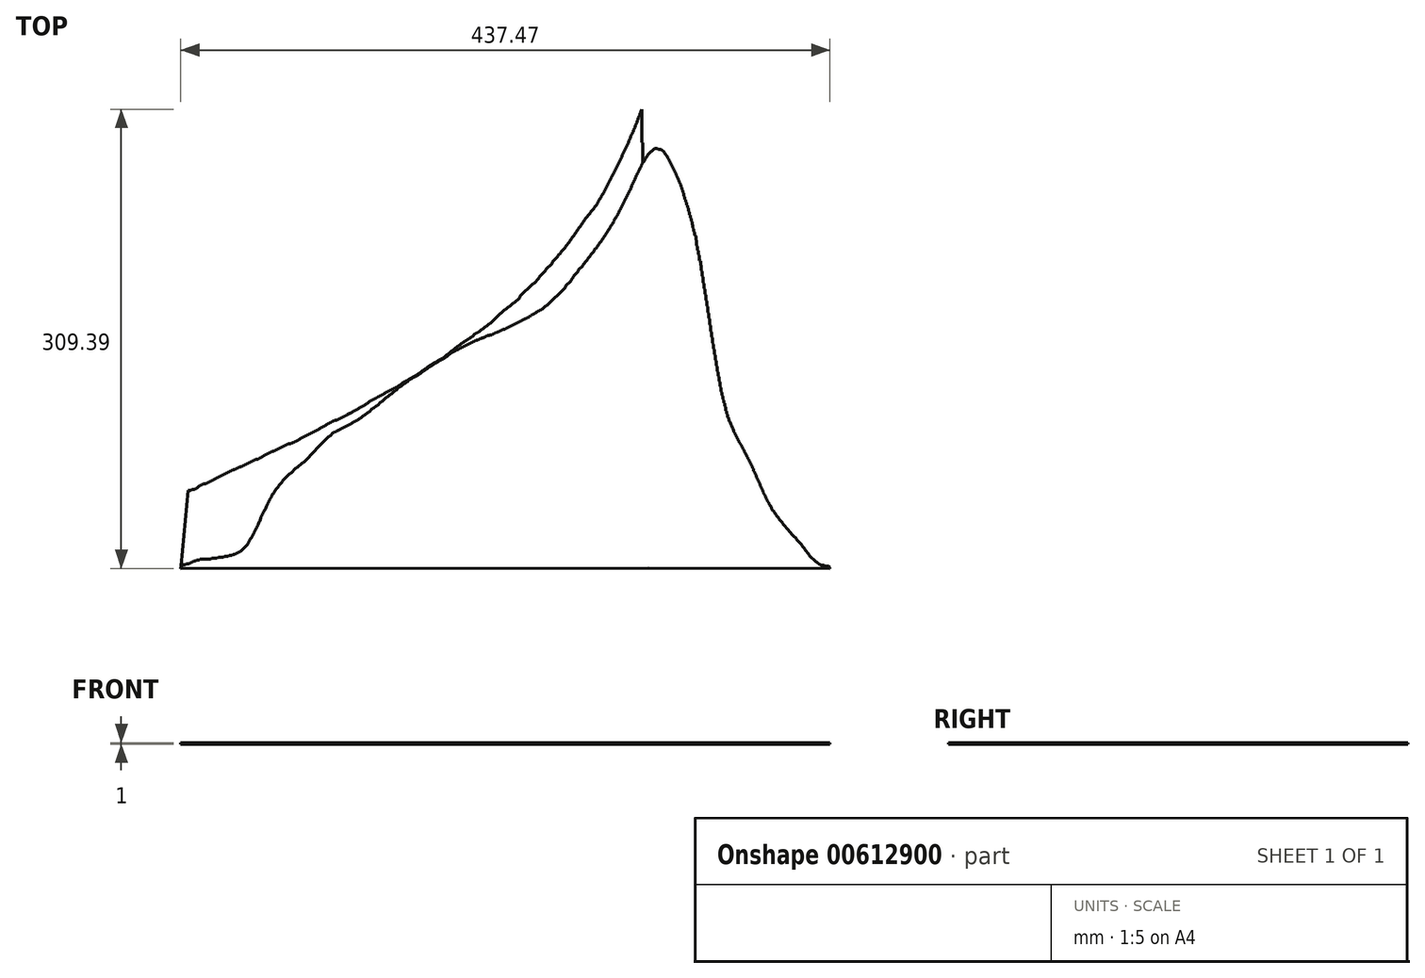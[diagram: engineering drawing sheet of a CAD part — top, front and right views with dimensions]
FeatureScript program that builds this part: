
annotation { "Feature Type Name" : "Feature", "Feature Type Description" : "" }
export const myFeature = defineFeature(function(context is Context, id is Id, definition is map)
    precondition{}
    {
        {
            var Q0;
            Q0=qCreatedBy(makeId("Top.planeOp"),FACE);
            var sketch = newSketch(context, id + "F0", { "sketchPlane" : qUnion([Q0])});
            skLineSegment(sketch, "E0", {"start": v(51.13, 44.28) * mm, "end": v(56.13, 96.91) * mm});
            skLineSegment(sketch, "E1", {"start": v(56.13, 96.91) * mm, "end": v(58.05, 96.91) * mm});
            skLineSegment(sketch, "E2", {"start": v(58.05, 96.91) * mm, "end": v(58.66, 97.6) * mm});
            skLineSegment(sketch, "E3", {"start": v(58.66, 97.6) * mm, "end": v(60.56, 97.6) * mm});
            skLineSegment(sketch, "E4", {"start": v(60.56, 97.6) * mm, "end": v(61.2, 98.2) * mm});
            skLineSegment(sketch, "E5", {"start": v(61.2, 98.2) * mm, "end": v(61.81, 98.2) * mm});
            skLineSegment(sketch, "E6", {"start": v(61.81, 98.2) * mm, "end": v(63.7, 100.09) * mm});
            skLineSegment(sketch, "E7", {"start": v(63.7, 100.09) * mm, "end": v(64.32, 100.09) * mm});
            skLineSegment(sketch, "E8", {"start": v(64.32, 100.09) * mm, "end": v(64.95, 100.72) * mm});
            skLineSegment(sketch, "E9", {"start": v(64.95, 100.72) * mm, "end": v(65.58, 100.72) * mm});
            skLineSegment(sketch, "E10", {"start": v(65.58, 100.72) * mm, "end": v(66.2, 101.35) * mm});
            skLineSegment(sketch, "E11", {"start": v(66.2, 101.35) * mm, "end": v(68.08, 101.35) * mm});
            skLineSegment(sketch, "E12", {"start": v(68.08, 101.35) * mm, "end": v(68.71, 101.98) * mm});
            skLineSegment(sketch, "E13", {"start": v(68.71, 101.98) * mm, "end": v(69.35, 101.98) * mm});
            skLineSegment(sketch, "E14", {"start": v(69.35, 101.98) * mm, "end": v(69.97, 102.6) * mm});
            skLineSegment(sketch, "E15", {"start": v(69.97, 102.6) * mm, "end": v(70.6, 102.6) * mm});
            skLineSegment(sketch, "E16", {"start": v(70.6, 102.6) * mm, "end": v(71.23, 103.23) * mm});
            skLineSegment(sketch, "E17", {"start": v(71.23, 103.23) * mm, "end": v(71.85, 103.23) * mm});
            skLineSegment(sketch, "E18", {"start": v(71.85, 103.23) * mm, "end": v(72.48, 103.86) * mm});
            skLineSegment(sketch, "E19", {"start": v(72.48, 103.86) * mm, "end": v(73.11, 103.86) * mm});
            skLineSegment(sketch, "E20", {"start": v(73.11, 103.86) * mm, "end": v(73.73, 104.49) * mm});
            skLineSegment(sketch, "E21", {"start": v(73.73, 104.49) * mm, "end": v(74.35, 104.49) * mm});
            skLineSegment(sketch, "E22", {"start": v(74.35, 104.49) * mm, "end": v(74.98, 105.11) * mm});
            skLineSegment(sketch, "E23", {"start": v(74.98, 105.11) * mm, "end": v(75.62, 105.11) * mm});
            skLineSegment(sketch, "E24", {"start": v(75.62, 105.11) * mm, "end": v(76.24, 105.74) * mm});
            skLineSegment(sketch, "E25", {"start": v(76.24, 105.74) * mm, "end": v(76.87, 105.74) * mm});
            skLineSegment(sketch, "E26", {"start": v(76.87, 105.74) * mm, "end": v(77.49, 106.37) * mm});
            skLineSegment(sketch, "E27", {"start": v(77.49, 106.37) * mm, "end": v(78.12, 106.37) * mm});
            skLineSegment(sketch, "E28", {"start": v(78.12, 106.37) * mm, "end": v(78.75, 107) * mm});
            skLineSegment(sketch, "E29", {"start": v(78.75, 107) * mm, "end": v(79.39, 107) * mm});
            skLineSegment(sketch, "E30", {"start": v(79.39, 107) * mm, "end": v(80.01, 107.61) * mm});
            skLineSegment(sketch, "E31", {"start": v(80.01, 107.61) * mm, "end": v(80.64, 107.61) * mm});
            skLineSegment(sketch, "E32", {"start": v(80.64, 107.61) * mm, "end": v(81.29, 108.25) * mm});
            skLineSegment(sketch, "E33", {"start": v(81.29, 108.25) * mm, "end": v(81.89, 108.25) * mm});
            skLineSegment(sketch, "E34", {"start": v(81.89, 108.25) * mm, "end": v(82.52, 108.87) * mm});
            skLineSegment(sketch, "E35", {"start": v(82.52, 108.87) * mm, "end": v(83.14, 108.87) * mm});
            skLineSegment(sketch, "E36", {"start": v(83.14, 108.87) * mm, "end": v(83.78, 109.5) * mm});
            skLineSegment(sketch, "E37", {"start": v(83.78, 109.5) * mm, "end": v(84.4, 109.5) * mm});
            skLineSegment(sketch, "E38", {"start": v(84.4, 109.5) * mm, "end": v(85.03, 110.13) * mm});
            skLineSegment(sketch, "E39", {"start": v(85.03, 110.13) * mm, "end": v(85.65, 110.13) * mm});
            skLineSegment(sketch, "E40", {"start": v(85.65, 110.13) * mm, "end": v(86.3, 110.76) * mm});
            skLineSegment(sketch, "E41", {"start": v(86.3, 110.76) * mm, "end": v(87.53, 110.76) * mm});
            skLineSegment(sketch, "E42", {"start": v(87.53, 110.76) * mm, "end": v(88.16, 111.38) * mm});
            skLineSegment(sketch, "E43", {"start": v(88.16, 111.38) * mm, "end": v(88.8, 111.38) * mm});
            skLineSegment(sketch, "E44", {"start": v(88.8, 111.38) * mm, "end": v(89.44, 112.02) * mm});
            skLineSegment(sketch, "E45", {"start": v(89.44, 112.02) * mm, "end": v(90.05, 112.02) * mm});
            skLineSegment(sketch, "E46", {"start": v(90.05, 112.02) * mm, "end": v(90.68, 112.64) * mm});
            skLineSegment(sketch, "E47", {"start": v(90.68, 112.64) * mm, "end": v(91.93, 112.64) * mm});
            skLineSegment(sketch, "E48", {"start": v(91.93, 112.64) * mm, "end": v(92.56, 113.27) * mm});
            skLineSegment(sketch, "E49", {"start": v(92.56, 113.27) * mm, "end": v(93.19, 113.27) * mm});
            skLineSegment(sketch, "E50", {"start": v(93.19, 113.27) * mm, "end": v(93.83, 113.9) * mm});
            skLineSegment(sketch, "E51", {"start": v(93.83, 113.9) * mm, "end": v(94.45, 113.9) * mm});
            skLineSegment(sketch, "E52", {"start": v(94.45, 113.9) * mm, "end": v(95.07, 114.52) * mm});
            skLineSegment(sketch, "E53", {"start": v(95.07, 114.52) * mm, "end": v(95.7, 114.52) * mm});
            skLineSegment(sketch, "E54", {"start": v(95.7, 114.52) * mm, "end": v(96.33, 115.15) * mm});
            skLineSegment(sketch, "E55", {"start": v(96.33, 115.15) * mm, "end": v(96.96, 115.15) * mm});
            skLineSegment(sketch, "E56", {"start": v(96.96, 115.15) * mm, "end": v(97.59, 115.78) * mm});
            skLineSegment(sketch, "E57", {"start": v(97.59, 115.78) * mm, "end": v(98.21, 115.78) * mm});
            skLineSegment(sketch, "E58", {"start": v(98.21, 115.78) * mm, "end": v(98.85, 116.4) * mm});
            skLineSegment(sketch, "E59", {"start": v(98.85, 116.4) * mm, "end": v(99.47, 116.4) * mm});
            skLineSegment(sketch, "E60", {"start": v(99.47, 116.4) * mm, "end": v(100.12, 117.04) * mm});
            skLineSegment(sketch, "E61", {"start": v(100.12, 117.04) * mm, "end": v(100.72, 117.04) * mm});
            skLineSegment(sketch, "E62", {"start": v(100.72, 117.04) * mm, "end": v(101.36, 117.66) * mm});
            skLineSegment(sketch, "E63", {"start": v(101.36, 117.66) * mm, "end": v(103.25, 117.66) * mm});
            skLineSegment(sketch, "E64", {"start": v(103.25, 117.66) * mm, "end": v(103.84, 118.31) * mm});
            skLineSegment(sketch, "E65", {"start": v(103.84, 118.31) * mm, "end": v(104.5, 118.31) * mm});
            skLineSegment(sketch, "E66", {"start": v(104.5, 118.31) * mm, "end": v(105.12, 118.92) * mm});
            skLineSegment(sketch, "E67", {"start": v(105.12, 118.92) * mm, "end": v(105.74, 118.92) * mm});
            skLineSegment(sketch, "E68", {"start": v(105.74, 118.92) * mm, "end": v(107.64, 120.8) * mm});
            skLineSegment(sketch, "E69", {"start": v(107.64, 120.8) * mm, "end": v(108.25, 120.8) * mm});
            skLineSegment(sketch, "E70", {"start": v(108.25, 120.8) * mm, "end": v(108.88, 121.42) * mm});
            skLineSegment(sketch, "E71", {"start": v(108.88, 121.42) * mm, "end": v(109.5, 121.42) * mm});
            skLineSegment(sketch, "E72", {"start": v(109.5, 121.42) * mm, "end": v(110.14, 122.05) * mm});
            skLineSegment(sketch, "E73", {"start": v(110.14, 122.05) * mm, "end": v(110.75, 122.05) * mm});
            skLineSegment(sketch, "E74", {"start": v(110.75, 122.05) * mm, "end": v(111.39, 122.68) * mm});
            skLineSegment(sketch, "E75", {"start": v(111.39, 122.68) * mm, "end": v(112, 122.68) * mm});
            skLineSegment(sketch, "E76", {"start": v(112, 122.68) * mm, "end": v(112.66, 123.32) * mm});
            skLineSegment(sketch, "E77", {"start": v(112.66, 123.32) * mm, "end": v(113.9, 123.32) * mm});
            skLineSegment(sketch, "E78", {"start": v(113.9, 123.32) * mm, "end": v(114.53, 123.93) * mm});
            skLineSegment(sketch, "E79", {"start": v(114.53, 123.93) * mm, "end": v(115.15, 123.93) * mm});
            skLineSegment(sketch, "E80", {"start": v(115.15, 123.93) * mm, "end": v(115.8, 124.57) * mm});
            skLineSegment(sketch, "E81", {"start": v(115.8, 124.57) * mm, "end": v(116.41, 124.57) * mm});
            skLineSegment(sketch, "E82", {"start": v(116.41, 124.57) * mm, "end": v(117.05, 125.2) * mm});
            skLineSegment(sketch, "E83", {"start": v(117.05, 125.2) * mm, "end": v(117.66, 125.2) * mm});
            skLineSegment(sketch, "E84", {"start": v(117.66, 125.2) * mm, "end": v(118.3, 125.83) * mm});
            skLineSegment(sketch, "E85", {"start": v(118.3, 125.83) * mm, "end": v(118.92, 125.83) * mm});
            skLineSegment(sketch, "E86", {"start": v(118.92, 125.83) * mm, "end": v(119.55, 126.45) * mm});
            skLineSegment(sketch, "E87", {"start": v(119.55, 126.45) * mm, "end": v(120.2, 126.45) * mm});
            skLineSegment(sketch, "E88", {"start": v(120.2, 126.45) * mm, "end": v(120.84, 127.08) * mm});
            skLineSegment(sketch, "E89", {"start": v(120.84, 127.08) * mm, "end": v(121.44, 127.08) * mm});
            skLineSegment(sketch, "E90", {"start": v(121.44, 127.08) * mm, "end": v(122.07, 127.7) * mm});
            skLineSegment(sketch, "E91", {"start": v(122.07, 127.7) * mm, "end": v(122.7, 127.7) * mm});
            skLineSegment(sketch, "E92", {"start": v(122.7, 127.7) * mm, "end": v(123.34, 128.34) * mm});
            skLineSegment(sketch, "E93", {"start": v(123.34, 128.34) * mm, "end": v(125.2, 128.34) * mm});
            skLineSegment(sketch, "E94", {"start": v(125.2, 128.34) * mm, "end": v(125.83, 128.97) * mm});
            skLineSegment(sketch, "E95", {"start": v(125.83, 128.97) * mm, "end": v(127.06, 128.97) * mm});
            skLineSegment(sketch, "E96", {"start": v(127.06, 128.97) * mm, "end": v(127.69, 129.58) * mm});
            skLineSegment(sketch, "E97", {"start": v(127.69, 129.58) * mm, "end": v(128.34, 129.58) * mm});
            skLineSegment(sketch, "E98", {"start": v(128.34, 129.58) * mm, "end": v(128.97, 130.2) * mm});
            skLineSegment(sketch, "E99", {"start": v(128.97, 130.2) * mm, "end": v(129.6, 130.2) * mm});
            skLineSegment(sketch, "E100", {"start": v(129.6, 130.2) * mm, "end": v(130.23, 130.83) * mm});
            skLineSegment(sketch, "E101", {"start": v(130.23, 130.83) * mm, "end": v(130.84, 130.83) * mm});
            skLineSegment(sketch, "E102", {"start": v(130.84, 130.83) * mm, "end": v(132.1, 132.08) * mm});
            skLineSegment(sketch, "E103", {"start": v(132.1, 132.08) * mm, "end": v(132.72, 132.08) * mm});
            skLineSegment(sketch, "E104", {"start": v(132.72, 132.08) * mm, "end": v(133.36, 132.72) * mm});
            skLineSegment(sketch, "E105", {"start": v(133.36, 132.72) * mm, "end": v(133.98, 132.72) * mm});
            skLineSegment(sketch, "E106", {"start": v(133.98, 132.72) * mm, "end": v(134.62, 133.35) * mm});
            skLineSegment(sketch, "E107", {"start": v(134.62, 133.35) * mm, "end": v(135.26, 133.35) * mm});
            skLineSegment(sketch, "E108", {"start": v(135.26, 133.35) * mm, "end": v(135.85, 134) * mm});
            skLineSegment(sketch, "E109", {"start": v(135.85, 134) * mm, "end": v(136.5, 134) * mm});
            skLineSegment(sketch, "E110", {"start": v(136.5, 134) * mm, "end": v(137.06, 134.62) * mm});
            skLineSegment(sketch, "E111", {"start": v(137.06, 134.62) * mm, "end": v(137.76, 134.62) * mm});
            skLineSegment(sketch, "E112", {"start": v(137.76, 134.62) * mm, "end": v(138.34, 135.25) * mm});
            skLineSegment(sketch, "E113", {"start": v(138.34, 135.25) * mm, "end": v(139, 135.25) * mm});
            skLineSegment(sketch, "E114", {"start": v(139, 135.25) * mm, "end": v(139.62, 135.86) * mm});
            skLineSegment(sketch, "E115", {"start": v(139.62, 135.86) * mm, "end": v(140.28, 135.86) * mm});
            skLineSegment(sketch, "E116", {"start": v(140.28, 135.86) * mm, "end": v(140.9, 136.53) * mm});
            skLineSegment(sketch, "E117", {"start": v(140.9, 136.53) * mm, "end": v(141.5, 136.53) * mm});
            skLineSegment(sketch, "E118", {"start": v(141.5, 136.53) * mm, "end": v(142.12, 137.13) * mm});
            skLineSegment(sketch, "E119", {"start": v(142.12, 137.13) * mm, "end": v(142.77, 137.13) * mm});
            skLineSegment(sketch, "E120", {"start": v(142.77, 137.13) * mm, "end": v(143.39, 137.74) * mm});
            skLineSegment(sketch, "E121", {"start": v(143.39, 137.74) * mm, "end": v(144.05, 137.74) * mm});
            skLineSegment(sketch, "E122", {"start": v(144.05, 137.74) * mm, "end": v(145.29, 139.01) * mm});
            skLineSegment(sketch, "E123", {"start": v(145.29, 139.01) * mm, "end": v(145.9, 139.01) * mm});
            skLineSegment(sketch, "E124", {"start": v(145.9, 139.01) * mm, "end": v(146.54, 139.63) * mm});
            skLineSegment(sketch, "E125", {"start": v(146.54, 139.63) * mm, "end": v(147.16, 139.63) * mm});
            skLineSegment(sketch, "E126", {"start": v(147.16, 139.63) * mm, "end": v(147.79, 140.26) * mm});
            skLineSegment(sketch, "E127", {"start": v(147.79, 140.26) * mm, "end": v(148.44, 140.26) * mm});
            skLineSegment(sketch, "E128", {"start": v(148.44, 140.26) * mm, "end": v(149.7, 141.5) * mm});
            skLineSegment(sketch, "E129", {"start": v(149.7, 141.5) * mm, "end": v(150.28, 141.5) * mm});
            skLineSegment(sketch, "E130", {"start": v(150.28, 141.5) * mm, "end": v(150.93, 142.14) * mm});
            skLineSegment(sketch, "E131", {"start": v(150.93, 142.14) * mm, "end": v(151.63, 142.14) * mm});
            skLineSegment(sketch, "E132", {"start": v(151.63, 142.14) * mm, "end": v(152.22, 142.8) * mm});
            skLineSegment(sketch, "E133", {"start": v(152.22, 142.8) * mm, "end": v(152.86, 142.8) * mm});
            skLineSegment(sketch, "E134", {"start": v(152.86, 142.8) * mm, "end": v(153.4, 143.38) * mm});
            skLineSegment(sketch, "E135", {"start": v(153.4, 143.38) * mm, "end": v(154.1, 143.38) * mm});
            skLineSegment(sketch, "E136", {"start": v(154.1, 143.38) * mm, "end": v(154.71, 144.06) * mm});
            skLineSegment(sketch, "E137", {"start": v(154.71, 144.06) * mm, "end": v(156.57, 144.06) * mm});
            skLineSegment(sketch, "E138", {"start": v(156.57, 144.06) * mm, "end": v(157.17, 144.66) * mm});
            skLineSegment(sketch, "E139", {"start": v(157.17, 144.66) * mm, "end": v(157.82, 144.66) * mm});
            skLineSegment(sketch, "E140", {"start": v(157.82, 144.66) * mm, "end": v(158.46, 145.29) * mm});
            skLineSegment(sketch, "E141", {"start": v(158.46, 145.29) * mm, "end": v(159.07, 145.29) * mm});
            skLineSegment(sketch, "E142", {"start": v(159.07, 145.29) * mm, "end": v(159.7, 145.91) * mm});
            skLineSegment(sketch, "E143", {"start": v(159.7, 145.91) * mm, "end": v(160.34, 145.91) * mm});
            skLineSegment(sketch, "E144", {"start": v(160.34, 145.91) * mm, "end": v(160.98, 146.54) * mm});
            skLineSegment(sketch, "E145", {"start": v(160.98, 146.54) * mm, "end": v(161.6, 146.54) * mm});
            skLineSegment(sketch, "E146", {"start": v(161.6, 146.54) * mm, "end": v(162.85, 147.78) * mm});
            skLineSegment(sketch, "E147", {"start": v(162.85, 147.78) * mm, "end": v(163.47, 147.78) * mm});
            skLineSegment(sketch, "E148", {"start": v(163.47, 147.78) * mm, "end": v(164.09, 148.46) * mm});
            skLineSegment(sketch, "E149", {"start": v(164.09, 148.46) * mm, "end": v(164.72, 148.46) * mm});
            skLineSegment(sketch, "E150", {"start": v(164.72, 148.46) * mm, "end": v(165.31, 149.05) * mm});
            skLineSegment(sketch, "E151", {"start": v(165.31, 149.05) * mm, "end": v(166.02, 149.05) * mm});
            skLineSegment(sketch, "E152", {"start": v(166.02, 149.05) * mm, "end": v(167.25, 150.26) * mm});
            skLineSegment(sketch, "E153", {"start": v(167.25, 150.26) * mm, "end": v(167.87, 150.26) * mm});
            skLineSegment(sketch, "E154", {"start": v(167.87, 150.26) * mm, "end": v(168.54, 150.92) * mm});
            skLineSegment(sketch, "E155", {"start": v(168.54, 150.92) * mm, "end": v(169.12, 150.92) * mm});
            skLineSegment(sketch, "E156", {"start": v(169.12, 150.92) * mm, "end": v(169.75, 151.54) * mm});
            skLineSegment(sketch, "E157", {"start": v(169.75, 151.54) * mm, "end": v(170.38, 151.54) * mm});
            skLineSegment(sketch, "E158", {"start": v(170.38, 151.54) * mm, "end": v(171.68, 152.83) * mm});
            skLineSegment(sketch, "E159", {"start": v(171.68, 152.83) * mm, "end": v(172.28, 152.83) * mm});
            skLineSegment(sketch, "E160", {"start": v(172.28, 152.83) * mm, "end": v(172.9, 153.44) * mm});
            skLineSegment(sketch, "E161", {"start": v(172.9, 153.44) * mm, "end": v(173.52, 153.44) * mm});
            skLineSegment(sketch, "E162", {"start": v(173.52, 153.44) * mm, "end": v(174.15, 154.06) * mm});
            skLineSegment(sketch, "E163", {"start": v(174.15, 154.06) * mm, "end": v(174.78, 154.06) * mm});
            skLineSegment(sketch, "E164", {"start": v(174.78, 154.06) * mm, "end": v(176.04, 155.3) * mm});
            skLineSegment(sketch, "E165", {"start": v(176.04, 155.3) * mm, "end": v(176.66, 155.3) * mm});
            skLineSegment(sketch, "E166", {"start": v(176.66, 155.3) * mm, "end": v(178.56, 157.19) * mm});
            skLineSegment(sketch, "E167", {"start": v(178.56, 157.19) * mm, "end": v(179.18, 157.19) * mm});
            skLineSegment(sketch, "E168", {"start": v(179.18, 157.19) * mm, "end": v(179.83, 157.83) * mm});
            skLineSegment(sketch, "E169", {"start": v(179.83, 157.83) * mm, "end": v(180.43, 157.83) * mm});
            skLineSegment(sketch, "E170", {"start": v(180.43, 157.83) * mm, "end": v(181.07, 158.46) * mm});
            skLineSegment(sketch, "E171", {"start": v(181.07, 158.46) * mm, "end": v(181.7, 158.46) * mm});
            skLineSegment(sketch, "E172", {"start": v(181.7, 158.46) * mm, "end": v(182.31, 159.07) * mm});
            skLineSegment(sketch, "E173", {"start": v(182.31, 159.07) * mm, "end": v(182.95, 159.07) * mm});
            skLineSegment(sketch, "E174", {"start": v(182.95, 159.07) * mm, "end": v(183.57, 159.69) * mm});
            skLineSegment(sketch, "E175", {"start": v(183.57, 159.69) * mm, "end": v(184.21, 159.69) * mm});
            skLineSegment(sketch, "E176", {"start": v(184.21, 159.69) * mm, "end": v(184.8, 160.34) * mm});
            skLineSegment(sketch, "E177", {"start": v(184.8, 160.34) * mm, "end": v(185.43, 160.34) * mm});
            skLineSegment(sketch, "E178", {"start": v(185.43, 160.34) * mm, "end": v(186.07, 160.97) * mm});
            skLineSegment(sketch, "E179", {"start": v(186.07, 160.97) * mm, "end": v(186.73, 160.97) * mm});
            skLineSegment(sketch, "E180", {"start": v(186.73, 160.97) * mm, "end": v(187.31, 161.6) * mm});
            skLineSegment(sketch, "E181", {"start": v(187.31, 161.6) * mm, "end": v(187.94, 161.6) * mm});
            skLineSegment(sketch, "E182", {"start": v(187.94, 161.6) * mm, "end": v(189.2, 162.86) * mm});
            skLineSegment(sketch, "E183", {"start": v(189.2, 162.86) * mm, "end": v(189.86, 162.86) * mm});
            skLineSegment(sketch, "E184", {"start": v(189.86, 162.86) * mm, "end": v(190.42, 163.47) * mm});
            skLineSegment(sketch, "E185", {"start": v(190.42, 163.47) * mm, "end": v(191.12, 163.47) * mm});
            skLineSegment(sketch, "E186", {"start": v(191.12, 163.47) * mm, "end": v(191.75, 164.1) * mm});
            skLineSegment(sketch, "E187", {"start": v(191.75, 164.1) * mm, "end": v(192.37, 164.1) * mm});
            skLineSegment(sketch, "E188", {"start": v(192.37, 164.1) * mm, "end": v(192.99, 164.7) * mm});
            skLineSegment(sketch, "E189", {"start": v(192.99, 164.7) * mm, "end": v(193.6, 164.7) * mm});
            skLineSegment(sketch, "E190", {"start": v(193.6, 164.7) * mm, "end": v(194.23, 165.37) * mm});
            skLineSegment(sketch, "E191", {"start": v(194.23, 165.37) * mm, "end": v(194.86, 165.37) * mm});
            skLineSegment(sketch, "E192", {"start": v(194.86, 165.37) * mm, "end": v(195.48, 165.98) * mm});
            skLineSegment(sketch, "E193", {"start": v(195.48, 165.98) * mm, "end": v(196.14, 165.98) * mm});
            skLineSegment(sketch, "E194", {"start": v(196.14, 165.98) * mm, "end": v(196.74, 166.58) * mm});
            skLineSegment(sketch, "E195", {"start": v(196.74, 166.58) * mm, "end": v(197.4, 166.58) * mm});
            skLineSegment(sketch, "E196", {"start": v(197.4, 166.58) * mm, "end": v(198.61, 167.9) * mm});
            skLineSegment(sketch, "E197", {"start": v(198.61, 167.9) * mm, "end": v(199.24, 167.9) * mm});
            skLineSegment(sketch, "E198", {"start": v(199.24, 167.9) * mm, "end": v(201.15, 169.8) * mm});
            skLineSegment(sketch, "E199", {"start": v(201.15, 169.8) * mm, "end": v(201.76, 169.8) * mm});
            skLineSegment(sketch, "E200", {"start": v(201.76, 169.8) * mm, "end": v(202.37, 170.4) * mm});
            skLineSegment(sketch, "E201", {"start": v(202.37, 170.4) * mm, "end": v(203, 170.4) * mm});
            skLineSegment(sketch, "E202", {"start": v(203, 170.4) * mm, "end": v(203.63, 171.01) * mm});
            skLineSegment(sketch, "E203", {"start": v(203.63, 171.01) * mm, "end": v(204.29, 171.01) * mm});
            skLineSegment(sketch, "E204", {"start": v(204.29, 171.01) * mm, "end": v(204.89, 171.67) * mm});
            skLineSegment(sketch, "E205", {"start": v(204.89, 171.67) * mm, "end": v(206.15, 172.26) * mm});
            skLineSegment(sketch, "E206", {"start": v(206.15, 172.26) * mm, "end": v(209.28, 174.13) * mm});
            skLineSegment(sketch, "E207", {"start": v(209.28, 174.13) * mm, "end": v(209.9, 174.76) * mm});
            skLineSegment(sketch, "E208", {"start": v(209.9, 174.76) * mm, "end": v(210.54, 174.76) * mm});
            skLineSegment(sketch, "E209", {"start": v(210.54, 174.76) * mm, "end": v(211.19, 175.4) * mm});
            skLineSegment(sketch, "E210", {"start": v(211.19, 175.4) * mm, "end": v(211.82, 176.02) * mm});
            skLineSegment(sketch, "E211", {"start": v(211.82, 176.02) * mm, "end": v(212.42, 176.02) * mm});
            skLineSegment(sketch, "E212", {"start": v(212.42, 176.02) * mm, "end": v(214.33, 177.9) * mm});
            skLineSegment(sketch, "E213", {"start": v(214.33, 177.9) * mm, "end": v(214.95, 177.9) * mm});
            skLineSegment(sketch, "E214", {"start": v(214.95, 177.9) * mm, "end": v(216.22, 179.15) * mm});
            skLineSegment(sketch, "E215", {"start": v(216.22, 179.15) * mm, "end": v(216.9, 179.15) * mm});
            skLineSegment(sketch, "E216", {"start": v(216.9, 179.15) * mm, "end": v(217.5, 179.8) * mm});
            skLineSegment(sketch, "E217", {"start": v(217.5, 179.8) * mm, "end": v(222.46, 182.92) * mm});
            skLineSegment(sketch, "E218", {"start": v(222.46, 182.92) * mm, "end": v(223.1, 183.55) * mm});
            skLineSegment(sketch, "E219", {"start": v(223.1, 183.55) * mm, "end": v(223.72, 183.55) * mm});
            skLineSegment(sketch, "E220", {"start": v(223.72, 183.55) * mm, "end": v(224.35, 184.18) * mm});
            skLineSegment(sketch, "E221", {"start": v(224.35, 184.18) * mm, "end": v(224.98, 184.8) * mm});
            skLineSegment(sketch, "E222", {"start": v(224.98, 184.8) * mm, "end": v(225.62, 184.8) * mm});
            skLineSegment(sketch, "E223", {"start": v(225.62, 184.8) * mm, "end": v(226.22, 185.45) * mm});
            skLineSegment(sketch, "E224", {"start": v(226.22, 185.45) * mm, "end": v(226.91, 185.45) * mm});
            skLineSegment(sketch, "E225", {"start": v(226.91, 185.45) * mm, "end": v(227.47, 186.07) * mm});
            skLineSegment(sketch, "E226", {"start": v(227.47, 186.07) * mm, "end": v(228.15, 186.07) * mm});
            skLineSegment(sketch, "E227", {"start": v(228.15, 186.07) * mm, "end": v(230.65, 188.55) * mm});
            skLineSegment(sketch, "E228", {"start": v(230.65, 188.55) * mm, "end": v(231.26, 188.55) * mm});
            skLineSegment(sketch, "E229", {"start": v(231.26, 188.55) * mm, "end": v(233.8, 191.06) * mm});
            skLineSegment(sketch, "E230", {"start": v(233.8, 191.06) * mm, "end": v(234.43, 191.06) * mm});
            skLineSegment(sketch, "E231", {"start": v(234.43, 191.06) * mm, "end": v(236.32, 192.94) * mm});
            skLineSegment(sketch, "E232", {"start": v(236.32, 192.94) * mm, "end": v(236.88, 192.94) * mm});
            skLineSegment(sketch, "E233", {"start": v(236.88, 192.94) * mm, "end": v(238.16, 194.2) * mm});
            skLineSegment(sketch, "E234", {"start": v(238.16, 194.2) * mm, "end": v(238.8, 194.2) * mm});
            skLineSegment(sketch, "E235", {"start": v(238.8, 194.2) * mm, "end": v(240.7, 196.08) * mm});
            skLineSegment(sketch, "E236", {"start": v(240.7, 196.08) * mm, "end": v(241.32, 196.08) * mm});
            skLineSegment(sketch, "E237", {"start": v(241.32, 196.08) * mm, "end": v(242.6, 197.35) * mm});
            skLineSegment(sketch, "E238", {"start": v(242.6, 197.35) * mm, "end": v(243.17, 197.35) * mm});
            skLineSegment(sketch, "E239", {"start": v(243.17, 197.35) * mm, "end": v(245.06, 199.22) * mm});
            skLineSegment(sketch, "E240", {"start": v(245.06, 199.22) * mm, "end": v(245.69, 199.22) * mm});
            skLineSegment(sketch, "E241", {"start": v(245.69, 199.22) * mm, "end": v(246.96, 200.47) * mm});
            skLineSegment(sketch, "E242", {"start": v(246.96, 200.47) * mm, "end": v(247.56, 200.47) * mm});
            skLineSegment(sketch, "E243", {"start": v(247.56, 200.47) * mm, "end": v(249.52, 202.4) * mm});
            skLineSegment(sketch, "E244", {"start": v(249.52, 202.4) * mm, "end": v(250.12, 202.4) * mm});
            skLineSegment(sketch, "E245", {"start": v(250.12, 202.4) * mm, "end": v(251.21, 203.6) * mm});
            skLineSegment(sketch, "E246", {"start": v(251.21, 203.6) * mm, "end": v(251.98, 203.6) * mm});
            skLineSegment(sketch, "E247", {"start": v(251.98, 203.6) * mm, "end": v(253.9, 205.51) * mm});
            skLineSegment(sketch, "E248", {"start": v(253.9, 205.51) * mm, "end": v(254.49, 205.51) * mm});
            skLineSegment(sketch, "E249", {"start": v(254.49, 205.51) * mm, "end": v(256.39, 207.39) * mm});
            skLineSegment(sketch, "E250", {"start": v(256.39, 207.39) * mm, "end": v(257, 207.39) * mm});
            skLineSegment(sketch, "E251", {"start": v(257, 207.39) * mm, "end": v(258.9, 209.26) * mm});
            skLineSegment(sketch, "E252", {"start": v(258.9, 209.26) * mm, "end": v(259.48, 209.26) * mm});
            skLineSegment(sketch, "E253", {"start": v(259.48, 209.26) * mm, "end": v(266.45, 216.16) * mm});
            skLineSegment(sketch, "E254", {"start": v(266.45, 216.16) * mm, "end": v(267, 216.16) * mm});
            skLineSegment(sketch, "E255", {"start": v(267, 216.16) * mm, "end": v(269.56, 218.69) * mm});
            skLineSegment(sketch, "E256", {"start": v(269.56, 218.69) * mm, "end": v(270.16, 218.69) * mm});
            skLineSegment(sketch, "E257", {"start": v(270.16, 218.69) * mm, "end": v(272.06, 220.56) * mm});
            skLineSegment(sketch, "E258", {"start": v(272.06, 220.56) * mm, "end": v(272.7, 220.56) * mm});
            skLineSegment(sketch, "E259", {"start": v(272.7, 220.56) * mm, "end": v(275.25, 223.08) * mm});
            skLineSegment(sketch, "E260", {"start": v(275.25, 223.08) * mm, "end": v(275.85, 223.08) * mm});
            skLineSegment(sketch, "E261", {"start": v(275.85, 223.08) * mm, "end": v(279.62, 226.8) * mm});
            skLineSegment(sketch, "E262", {"start": v(279.62, 226.8) * mm, "end": v(279.62, 227.55) * mm});
            skLineSegment(sketch, "E263", {"start": v(279.62, 227.55) * mm, "end": v(288.37, 236.2) * mm});
            skLineSegment(sketch, "E264", {"start": v(288.37, 236.2) * mm, "end": v(289.01, 236.2) * mm});
            skLineSegment(sketch, "E265", {"start": v(289.01, 236.2) * mm, "end": v(292.81, 239.95) * mm});
            skLineSegment(sketch, "E266", {"start": v(292.81, 239.95) * mm, "end": v(292.81, 240.78) * mm});
            skLineSegment(sketch, "E267", {"start": v(292.81, 240.78) * mm, "end": v(297.15, 245.06) * mm});
            skLineSegment(sketch, "E268", {"start": v(297.15, 245.06) * mm, "end": v(297.15, 245.73) * mm});
            skLineSegment(sketch, "E269", {"start": v(297.15, 245.73) * mm, "end": v(301.5, 250.03) * mm});
            skLineSegment(sketch, "E270", {"start": v(301.5, 250.03) * mm, "end": v(301.5, 250.76) * mm});
            skLineSegment(sketch, "E271", {"start": v(301.5, 250.76) * mm, "end": v(305.28, 254.5) * mm});
            skLineSegment(sketch, "E272", {"start": v(305.28, 254.5) * mm, "end": v(305.28, 255.13) * mm});
            skLineSegment(sketch, "E273", {"start": v(305.28, 255.13) * mm, "end": v(307.15, 256.97) * mm});
            skLineSegment(sketch, "E274", {"start": v(307.15, 256.97) * mm, "end": v(307.15, 257.65) * mm});
            skLineSegment(sketch, "E275", {"start": v(307.15, 257.65) * mm, "end": v(310.28, 260.74) * mm});
            skLineSegment(sketch, "E276", {"start": v(310.28, 260.74) * mm, "end": v(310.28, 261.43) * mm});
            skLineSegment(sketch, "E277", {"start": v(310.28, 261.43) * mm, "end": v(313.42, 264.53) * mm});
            skLineSegment(sketch, "E278", {"start": v(313.42, 264.53) * mm, "end": v(313.42, 265.18) * mm});
            skLineSegment(sketch, "E279", {"start": v(313.42, 265.18) * mm, "end": v(314.66, 266.4) * mm});
            skLineSegment(sketch, "E280", {"start": v(314.66, 266.4) * mm, "end": v(314.66, 267.07) * mm});
            skLineSegment(sketch, "E281", {"start": v(314.66, 267.07) * mm, "end": v(316.54, 268.93) * mm});
            skLineSegment(sketch, "E282", {"start": v(316.54, 268.93) * mm, "end": v(316.54, 269.54) * mm});
            skLineSegment(sketch, "E283", {"start": v(316.54, 269.54) * mm, "end": v(317.85, 270.83) * mm});
            skLineSegment(sketch, "E284", {"start": v(317.85, 270.83) * mm, "end": v(317.85, 271.45) * mm});
            skLineSegment(sketch, "E285", {"start": v(317.85, 271.45) * mm, "end": v(319.08, 272.66) * mm});
            skLineSegment(sketch, "E286", {"start": v(319.08, 272.66) * mm, "end": v(319.08, 273.35) * mm});
            skLineSegment(sketch, "E287", {"start": v(319.08, 273.35) * mm, "end": v(320.97, 275.22) * mm});
            skLineSegment(sketch, "E288", {"start": v(320.97, 275.22) * mm, "end": v(320.97, 275.85) * mm});
            skLineSegment(sketch, "E289", {"start": v(320.97, 275.85) * mm, "end": v(322.2, 277.07) * mm});
            skLineSegment(sketch, "E290", {"start": v(322.2, 277.07) * mm, "end": v(322.2, 277.68) * mm});
            skLineSegment(sketch, "E291", {"start": v(322.2, 277.68) * mm, "end": v(323.5, 278.95) * mm});
            skLineSegment(sketch, "E292", {"start": v(323.5, 278.95) * mm, "end": v(323.5, 279.64) * mm});
            skLineSegment(sketch, "E293", {"start": v(323.5, 279.64) * mm, "end": v(325.36, 281.48) * mm});
            skLineSegment(sketch, "E294", {"start": v(325.36, 281.48) * mm, "end": v(325.36, 282.09) * mm});
            skLineSegment(sketch, "E295", {"start": v(325.36, 282.09) * mm, "end": v(327.25, 283.96) * mm});
            skLineSegment(sketch, "E296", {"start": v(327.25, 283.96) * mm, "end": v(327.25, 284.63) * mm});
            skLineSegment(sketch, "E297", {"start": v(327.25, 284.63) * mm, "end": v(329.77, 287.12) * mm});
            skLineSegment(sketch, "E298", {"start": v(329.77, 287.12) * mm, "end": v(329.77, 287.75) * mm});
            skLineSegment(sketch, "E299", {"start": v(329.77, 287.75) * mm, "end": v(331.62, 289.58) * mm});
            skLineSegment(sketch, "E300", {"start": v(331.62, 289.58) * mm, "end": v(331.62, 290.27) * mm});
            skLineSegment(sketch, "E301", {"start": v(331.62, 290.27) * mm, "end": v(332.27, 290.92) * mm});
            skLineSegment(sketch, "E302", {"start": v(332.27, 290.92) * mm, "end": v(332.27, 291.5) * mm});
            skLineSegment(sketch, "E303", {"start": v(332.27, 291.5) * mm, "end": v(332.86, 292.14) * mm});
            skLineSegment(sketch, "E304", {"start": v(332.86, 292.14) * mm, "end": v(332.86, 292.87) * mm});
            skLineSegment(sketch, "E305", {"start": v(332.86, 292.87) * mm, "end": v(334.11, 294.11) * mm});
            skLineSegment(sketch, "E306", {"start": v(334.11, 294.11) * mm, "end": v(334.11, 294.64) * mm});
            skLineSegment(sketch, "E307", {"start": v(334.11, 294.64) * mm, "end": v(334.8, 295.32) * mm});
            skLineSegment(sketch, "E308", {"start": v(334.8, 295.32) * mm, "end": v(334.8, 295.96) * mm});
            skLineSegment(sketch, "E309", {"start": v(334.8, 295.96) * mm, "end": v(336.01, 297.16) * mm});
            skLineSegment(sketch, "E310", {"start": v(336.01, 297.16) * mm, "end": v(336.01, 297.8) * mm});
            skLineSegment(sketch, "E311", {"start": v(336.01, 297.8) * mm, "end": v(336.66, 298.44) * mm});
            skLineSegment(sketch, "E312", {"start": v(336.66, 298.44) * mm, "end": v(336.66, 299.05) * mm});
            skLineSegment(sketch, "E313", {"start": v(336.66, 299.05) * mm, "end": v(337.28, 299.67) * mm});
            skLineSegment(sketch, "E314", {"start": v(337.28, 299.67) * mm, "end": v(337.28, 300.26) * mm});
            skLineSegment(sketch, "E315", {"start": v(337.28, 300.26) * mm, "end": v(337.9, 300.93) * mm});
            skLineSegment(sketch, "E316", {"start": v(337.9, 300.93) * mm, "end": v(337.9, 301.55) * mm});
            skLineSegment(sketch, "E317", {"start": v(337.9, 301.55) * mm, "end": v(338.55, 302.2) * mm});
            skLineSegment(sketch, "E318", {"start": v(338.55, 302.2) * mm, "end": v(338.55, 302.8) * mm});
            skLineSegment(sketch, "E319", {"start": v(338.55, 302.8) * mm, "end": v(339.17, 303.5) * mm});
            skLineSegment(sketch, "E320", {"start": v(339.17, 303.5) * mm, "end": v(339.17, 304.16) * mm});
            skLineSegment(sketch, "E321", {"start": v(339.17, 304.16) * mm, "end": v(340.41, 305.38) * mm});
            skLineSegment(sketch, "E322", {"start": v(340.41, 305.38) * mm, "end": v(340.41, 306) * mm});
            skLineSegment(sketch, "E323", {"start": v(340.41, 306) * mm, "end": v(341.04, 306.62) * mm});
            skLineSegment(sketch, "E324", {"start": v(341.04, 306.62) * mm, "end": v(341.04, 307.17) * mm});
            skLineSegment(sketch, "E325", {"start": v(341.04, 307.17) * mm, "end": v(341.66, 307.85) * mm});
            skLineSegment(sketch, "E326", {"start": v(341.66, 307.85) * mm, "end": v(341.66, 308.45) * mm});
            skLineSegment(sketch, "E327", {"start": v(341.66, 308.45) * mm, "end": v(342.26, 309.1) * mm});
            skLineSegment(sketch, "E328", {"start": v(342.26, 309.1) * mm, "end": v(342.26, 309.67) * mm});
            skLineSegment(sketch, "E329", {"start": v(342.26, 309.67) * mm, "end": v(342.95, 310.35) * mm});
            skLineSegment(sketch, "E330", {"start": v(342.95, 310.35) * mm, "end": v(342.95, 310.98) * mm});
            skLineSegment(sketch, "E331", {"start": v(342.95, 310.98) * mm, "end": v(343.56, 311.59) * mm});
            skLineSegment(sketch, "E332", {"start": v(343.56, 311.59) * mm, "end": v(343.56, 312.2) * mm});
            skLineSegment(sketch, "E333", {"start": v(343.56, 312.2) * mm, "end": v(344.17, 312.86) * mm});
            skLineSegment(sketch, "E334", {"start": v(344.17, 312.86) * mm, "end": v(344.17, 313.43) * mm});
            skLineSegment(sketch, "E335", {"start": v(344.17, 313.43) * mm, "end": v(344.84, 314.1) * mm});
            skLineSegment(sketch, "E336", {"start": v(344.84, 314.1) * mm, "end": v(344.84, 314.74) * mm});
            skLineSegment(sketch, "E337", {"start": v(344.84, 314.74) * mm, "end": v(345.45, 315.34) * mm});
            skLineSegment(sketch, "E338", {"start": v(345.45, 315.34) * mm, "end": v(345.45, 315.98) * mm});
            skLineSegment(sketch, "E339", {"start": v(345.45, 315.98) * mm, "end": v(346.1, 316.62) * mm});
            skLineSegment(sketch, "E340", {"start": v(346.1, 316.62) * mm, "end": v(346.1, 317.26) * mm});
            skLineSegment(sketch, "E341", {"start": v(346.1, 317.26) * mm, "end": v(346.73, 317.89) * mm});
            skLineSegment(sketch, "E342", {"start": v(346.73, 317.89) * mm, "end": v(346.73, 318.48) * mm});
            skLineSegment(sketch, "E343", {"start": v(346.73, 318.48) * mm, "end": v(347.3, 319.12) * mm});
            skLineSegment(sketch, "E344", {"start": v(347.3, 319.12) * mm, "end": v(347.3, 319.8) * mm});
            skLineSegment(sketch, "E345", {"start": v(347.3, 319.8) * mm, "end": v(347.95, 320.42) * mm});
            skLineSegment(sketch, "E346", {"start": v(347.95, 320.42) * mm, "end": v(347.95, 321.05) * mm});
            skLineSegment(sketch, "E347", {"start": v(347.95, 321.05) * mm, "end": v(348.58, 321.68) * mm});
            skLineSegment(sketch, "E348", {"start": v(348.58, 321.68) * mm, "end": v(348.58, 322.95) * mm});
            skLineSegment(sketch, "E349", {"start": v(348.58, 322.95) * mm, "end": v(349.2, 323.51) * mm});
            skLineSegment(sketch, "E350", {"start": v(349.2, 323.51) * mm, "end": v(349.2, 324.16) * mm});
            skLineSegment(sketch, "E351", {"start": v(349.2, 324.16) * mm, "end": v(349.8, 324.76) * mm});
            skLineSegment(sketch, "E352", {"start": v(349.8, 324.76) * mm, "end": v(349.87, 325.43) * mm});
            skLineSegment(sketch, "E353", {"start": v(349.87, 325.43) * mm, "end": v(350.43, 326.04) * mm});
            skLineSegment(sketch, "E354", {"start": v(350.43, 326.04) * mm, "end": v(350.49, 326.64) * mm});
            skLineSegment(sketch, "E355", {"start": v(350.49, 326.64) * mm, "end": v(351.05, 327.26) * mm});
            skLineSegment(sketch, "E356", {"start": v(351.05, 327.26) * mm, "end": v(351.05, 327.95) * mm});
            skLineSegment(sketch, "E357", {"start": v(351.05, 327.95) * mm, "end": v(351.73, 328.53) * mm});
            skLineSegment(sketch, "E358", {"start": v(351.73, 328.53) * mm, "end": v(351.73, 329.17) * mm});
            skLineSegment(sketch, "E359", {"start": v(351.73, 329.17) * mm, "end": v(352.36, 329.78) * mm});
            skLineSegment(sketch, "E360", {"start": v(352.36, 329.78) * mm, "end": v(352.36, 330.44) * mm});
            skLineSegment(sketch, "E361", {"start": v(352.36, 330.44) * mm, "end": v(352.93, 331.08) * mm});
            skLineSegment(sketch, "E362", {"start": v(352.93, 331.08) * mm, "end": v(352.93, 332.28) * mm});
            skLineSegment(sketch, "E363", {"start": v(352.93, 332.28) * mm, "end": v(353.62, 332.91) * mm});
            skLineSegment(sketch, "E364", {"start": v(353.62, 332.91) * mm, "end": v(353.62, 333.59) * mm});
            skLineSegment(sketch, "E365", {"start": v(353.62, 333.59) * mm, "end": v(354.22, 334.18) * mm});
            skLineSegment(sketch, "E366", {"start": v(354.22, 334.18) * mm, "end": v(354.22, 335.45) * mm});
            skLineSegment(sketch, "E367", {"start": v(354.22, 335.45) * mm, "end": v(354.85, 336.07) * mm});
            skLineSegment(sketch, "E368", {"start": v(354.85, 336.07) * mm, "end": v(354.85, 336.73) * mm});
            skLineSegment(sketch, "E369", {"start": v(354.85, 336.73) * mm, "end": v(355.46, 337.28) * mm});
            skLineSegment(sketch, "E370", {"start": v(355.46, 337.28) * mm, "end": v(355.46, 337.98) * mm});
            skLineSegment(sketch, "E371", {"start": v(355.46, 337.98) * mm, "end": v(356.11, 338.58) * mm});
            skLineSegment(sketch, "E372", {"start": v(356.11, 338.58) * mm, "end": v(356.11, 339.82) * mm});
            skLineSegment(sketch, "E373", {"start": v(356.11, 339.82) * mm, "end": v(356.71, 340.48) * mm});
            skLineSegment(sketch, "E374", {"start": v(356.71, 340.48) * mm, "end": v(356.71, 341.08) * mm});
            skLineSegment(sketch, "E375", {"start": v(356.71, 341.08) * mm, "end": v(357.38, 341.75) * mm});
            skLineSegment(sketch, "E376", {"start": v(357.38, 341.75) * mm, "end": v(357.38, 342.95) * mm});
            skLineSegment(sketch, "E377", {"start": v(357.38, 342.95) * mm, "end": v(358, 343.63) * mm});
            skLineSegment(sketch, "E378", {"start": v(358, 343.63) * mm, "end": v(358, 344.13) * mm});
            skLineSegment(sketch, "E379", {"start": v(358, 344.13) * mm, "end": v(358.66, 344.85) * mm});
            skLineSegment(sketch, "E380", {"start": v(358.66, 344.85) * mm, "end": v(358.66, 346.12) * mm});
            skLineSegment(sketch, "E381", {"start": v(358.66, 346.12) * mm, "end": v(359.24, 346.77) * mm});
            skLineSegment(sketch, "E382", {"start": v(359.24, 346.77) * mm, "end": v(359.24, 347.95) * mm});
            skLineSegment(sketch, "E383", {"start": v(359.24, 347.95) * mm, "end": v(359.87, 348.64) * mm});
            skLineSegment(sketch, "E384", {"start": v(359.87, 348.64) * mm, "end": v(359.87, 349.24) * mm});
            skLineSegment(sketch, "E385", {"start": v(359.87, 349.24) * mm, "end": v(360.48, 349.91) * mm});
            skLineSegment(sketch, "E386", {"start": v(360.48, 349.91) * mm, "end": v(360.48, 351.1) * mm});
            skLineSegment(sketch, "E387", {"start": v(360.48, 351.1) * mm, "end": v(361.14, 351.76) * mm});
            skLineSegment(sketch, "E388", {"start": v(361.14, 351.76) * mm, "end": v(361.14, 352.35) * mm});
            skLineSegment(sketch, "E389", {"start": v(361.14, 352.35) * mm, "end": v(361.8, 353.67) * mm});
            skLineSegment(sketch, "E390", {"start": v(361.8, 353.67) * mm, "end": v(361.8, 331.6) * mm});
            skLineSegment(sketch, "E391", {"start": v(361.8, 331.6) * mm, "end": v(362.4, 331.02) * mm});
            skLineSegment(sketch, "E392", {"start": v(362.4, 331.02) * mm, "end": v(362.4, 287.75) * mm});
            skLineSegment(sketch, "E393", {"start": v(362.4, 287.75) * mm, "end": v(363.07, 287.07) * mm});
            skLineSegment(sketch, "E394", {"start": v(363.07, 287.07) * mm, "end": v(363.07, 243.25) * mm});
            skLineSegment(sketch, "E395", {"start": v(363.07, 243.25) * mm, "end": v(363.76, 242.56) * mm});
            skLineSegment(sketch, "E396", {"start": v(363.76, 242.56) * mm, "end": v(363.76, 199.28) * mm});
            skLineSegment(sketch, "E397", {"start": v(363.76, 199.28) * mm, "end": v(364.35, 198.67) * mm});
            skLineSegment(sketch, "E398", {"start": v(364.35, 198.67) * mm, "end": v(364.35, 155.3) * mm});
            skLineSegment(sketch, "E399", {"start": v(364.35, 155.3) * mm, "end": v(364.94, 154.65) * mm});
            skLineSegment(sketch, "E400", {"start": v(364.94, 154.65) * mm, "end": v(364.94, 110.76) * mm});
            skLineSegment(sketch, "E401", {"start": v(364.94, 110.76) * mm, "end": v(365.56, 110.13) * mm});
            skLineSegment(sketch, "E402", {"start": v(365.56, 110.13) * mm, "end": v(365.56, 67.02) * mm});
            skLineSegment(sketch, "E403", {"start": v(365.56, 67.02) * mm, "end": v(366.23, 66.34) * mm});
            skLineSegment(sketch, "E404", {"start": v(366.23, 66.34) * mm, "end": v(366.23, 44.34) * mm});
            skLineSegment(sketch, "E405", {"start": v(366.23, 44.34) * mm, "end": v(51.13, 44.28) * mm});
            skLineSegment(sketch, "E406", {"start": v(207.2, 172.89) * mm, "end": v(206.79, 172.27) * mm});
            skLineSegment(sketch, "E407", {"start": v(206.79, 172.27) * mm, "end": v(206.15, 171.63) * mm});
            skLineSegment(sketch, "E408", {"start": v(206.15, 171.63) * mm, "end": v(205.41, 171.63) * mm});
            skLineSegment(sketch, "E409", {"start": v(205.41, 171.63) * mm, "end": v(203.64, 169.76) * mm});
            skLineSegment(sketch, "E410", {"start": v(203.64, 169.76) * mm, "end": v(203.02, 169.76) * mm});
            skLineSegment(sketch, "E411", {"start": v(203.02, 169.76) * mm, "end": v(202.39, 169.11) * mm});
            skLineSegment(sketch, "E412", {"start": v(202.39, 169.11) * mm, "end": v(201.8, 168.51) * mm});
            skLineSegment(sketch, "E413", {"start": v(201.8, 168.51) * mm, "end": v(201.07, 168.51) * mm});
            skLineSegment(sketch, "E414", {"start": v(201.07, 168.51) * mm, "end": v(200.49, 167.83) * mm});
            skLineSegment(sketch, "E415", {"start": v(200.49, 167.83) * mm, "end": v(199.3, 166.61) * mm});
            skLineSegment(sketch, "E416", {"start": v(199.3, 166.61) * mm, "end": v(198.44, 166.61) * mm});
            skLineSegment(sketch, "E417", {"start": v(198.44, 166.61) * mm, "end": v(196.12, 164.12) * mm});
            skLineSegment(sketch, "E418", {"start": v(196.12, 164.12) * mm, "end": v(195.48, 164.12) * mm});
            skLineSegment(sketch, "E419", {"start": v(195.48, 164.12) * mm, "end": v(193.04, 161.6) * mm});
            skLineSegment(sketch, "E420", {"start": v(193.04, 161.6) * mm, "end": v(192.24, 161.6) * mm});
            skLineSegment(sketch, "E421", {"start": v(192.24, 161.6) * mm, "end": v(190.48, 159.71) * mm});
            skLineSegment(sketch, "E422", {"start": v(190.48, 159.71) * mm, "end": v(189.84, 159.71) * mm});
            skLineSegment(sketch, "E423", {"start": v(189.84, 159.71) * mm, "end": v(186.68, 156.58) * mm});
            skLineSegment(sketch, "E424", {"start": v(186.68, 156.58) * mm, "end": v(186.07, 156.58) * mm});
            skLineSegment(sketch, "E425", {"start": v(186.07, 156.58) * mm, "end": v(183.63, 154.05) * mm});
            skLineSegment(sketch, "E426", {"start": v(183.63, 154.05) * mm, "end": v(182.95, 154.05) * mm});
            skLineSegment(sketch, "E427", {"start": v(182.95, 154.05) * mm, "end": v(181.04, 152.17) * mm});
            skLineSegment(sketch, "E428", {"start": v(181.04, 152.17) * mm, "end": v(180.4, 152.17) * mm});
            skLineSegment(sketch, "E429", {"start": v(180.4, 152.17) * mm, "end": v(177.97, 149.66) * mm});
            skLineSegment(sketch, "E430", {"start": v(177.97, 149.66) * mm, "end": v(177.3, 149.66) * mm});
            skLineSegment(sketch, "E431", {"start": v(177.3, 149.66) * mm, "end": v(174.9, 147.18) * mm});
            skLineSegment(sketch, "E432", {"start": v(174.9, 147.18) * mm, "end": v(174.15, 147.18) * mm});
            skLineSegment(sketch, "E433", {"start": v(174.15, 147.18) * mm, "end": v(172.3, 145.27) * mm});
            skLineSegment(sketch, "E434", {"start": v(172.3, 145.27) * mm, "end": v(171.64, 145.27) * mm});
            skLineSegment(sketch, "E435", {"start": v(171.64, 145.27) * mm, "end": v(170.43, 144.02) * mm});
            skLineSegment(sketch, "E436", {"start": v(170.43, 144.02) * mm, "end": v(169.8, 144.02) * mm});
            skLineSegment(sketch, "E437", {"start": v(169.8, 144.02) * mm, "end": v(169.15, 143.36) * mm});
            skLineSegment(sketch, "E438", {"start": v(169.15, 143.36) * mm, "end": v(168.47, 143.36) * mm});
            skLineSegment(sketch, "E439", {"start": v(168.47, 143.36) * mm, "end": v(167.9, 142.76) * mm});
            skLineSegment(sketch, "E440", {"start": v(167.9, 142.76) * mm, "end": v(167.25, 142.76) * mm});
            skLineSegment(sketch, "E441", {"start": v(167.25, 142.76) * mm, "end": v(166.04, 141.51) * mm});
            skLineSegment(sketch, "E442", {"start": v(166.04, 141.51) * mm, "end": v(165.4, 141.51) * mm});
            skLineSegment(sketch, "E443", {"start": v(165.4, 141.51) * mm, "end": v(164.78, 140.87) * mm});
            skLineSegment(sketch, "E444", {"start": v(164.78, 140.87) * mm, "end": v(164.14, 140.87) * mm});
            skLineSegment(sketch, "E445", {"start": v(164.14, 140.87) * mm, "end": v(163.52, 140.23) * mm});
            skLineSegment(sketch, "E446", {"start": v(163.52, 140.23) * mm, "end": v(162.79, 140.23) * mm});
            skLineSegment(sketch, "E447", {"start": v(162.79, 140.23) * mm, "end": v(162.21, 139.64) * mm});
            skLineSegment(sketch, "E448", {"start": v(162.21, 139.64) * mm, "end": v(161.62, 139.64) * mm});
            skLineSegment(sketch, "E449", {"start": v(161.62, 139.64) * mm, "end": v(161.02, 139.01) * mm});
            skLineSegment(sketch, "E450", {"start": v(161.02, 139.01) * mm, "end": v(160.34, 139.01) * mm});
            skLineSegment(sketch, "E451", {"start": v(160.34, 139.01) * mm, "end": v(159.75, 138.4) * mm});
            skLineSegment(sketch, "E452", {"start": v(159.75, 138.4) * mm, "end": v(159.1, 138.4) * mm});
            skLineSegment(sketch, "E453", {"start": v(159.1, 138.4) * mm, "end": v(158.46, 137.74) * mm});
            skLineSegment(sketch, "E454", {"start": v(158.46, 137.74) * mm, "end": v(157.87, 137.74) * mm});
            skLineSegment(sketch, "E455", {"start": v(157.87, 137.74) * mm, "end": v(157.26, 137.11) * mm});
            skLineSegment(sketch, "E456", {"start": v(157.26, 137.11) * mm, "end": v(156.58, 137.11) * mm});
            skLineSegment(sketch, "E457", {"start": v(156.58, 137.11) * mm, "end": v(155.96, 136.47) * mm});
            skLineSegment(sketch, "E458", {"start": v(155.96, 136.47) * mm, "end": v(155.33, 136.47) * mm});
            skLineSegment(sketch, "E459", {"start": v(155.33, 136.47) * mm, "end": v(154.7, 135.87) * mm});
            skLineSegment(sketch, "E460", {"start": v(154.7, 135.87) * mm, "end": v(154, 135.87) * mm});
            skLineSegment(sketch, "E461", {"start": v(154, 135.87) * mm, "end": v(151.52, 133.31) * mm});
            skLineSegment(sketch, "E462", {"start": v(151.52, 133.31) * mm, "end": v(150.93, 133.31) * mm});
            skLineSegment(sketch, "E463", {"start": v(150.93, 133.31) * mm, "end": v(145.25, 127.68) * mm});
            skLineSegment(sketch, "E464", {"start": v(145.25, 127.68) * mm, "end": v(142.11, 124.58) * mm});
            skLineSegment(sketch, "E465", {"start": v(142.11, 124.58) * mm, "end": v(142.11, 124.02) * mm});
            skLineSegment(sketch, "E466", {"start": v(142.11, 124.02) * mm, "end": v(134.04, 115.67) * mm});
            skLineSegment(sketch, "E467", {"start": v(134.04, 115.67) * mm, "end": v(133.34, 115.67) * mm});
            skLineSegment(sketch, "E468", {"start": v(133.34, 115.67) * mm, "end": v(129.6, 111.96) * mm});
            skLineSegment(sketch, "E469", {"start": v(129.6, 111.96) * mm, "end": v(128.96, 111.96) * mm});
            skLineSegment(sketch, "E470", {"start": v(128.96, 111.96) * mm, "end": v(125.2, 108.23) * mm});
            skLineSegment(sketch, "E471", {"start": v(125.2, 108.23) * mm, "end": v(124.58, 108.23) * mm});
            skLineSegment(sketch, "E472", {"start": v(124.58, 108.23) * mm, "end": v(119.57, 103.27) * mm});
            skLineSegment(sketch, "E473", {"start": v(119.57, 103.27) * mm, "end": v(119.57, 102.55) * mm});
            skLineSegment(sketch, "E474", {"start": v(119.57, 102.55) * mm, "end": v(117.1, 100) * mm});
            skLineSegment(sketch, "E475", {"start": v(117.1, 100) * mm, "end": v(117.1, 99.44) * mm});
            skLineSegment(sketch, "E476", {"start": v(117.1, 99.44) * mm, "end": v(115.25, 97.6) * mm});
            skLineSegment(sketch, "E477", {"start": v(115.25, 97.6) * mm, "end": v(115.25, 97) * mm});
            skLineSegment(sketch, "E478", {"start": v(115.25, 97) * mm, "end": v(113.89, 95.6) * mm});
            skLineSegment(sketch, "E479", {"start": v(113.89, 95.6) * mm, "end": v(113.89, 94.8) * mm});
            skLineSegment(sketch, "E480", {"start": v(113.89, 94.8) * mm, "end": v(112.68, 94.08) * mm});
            skLineSegment(sketch, "E481", {"start": v(112.68, 94.08) * mm, "end": v(112.68, 93.13) * mm});
            skLineSegment(sketch, "E482", {"start": v(112.68, 93.13) * mm, "end": v(112.04, 92.5) * mm});
            skLineSegment(sketch, "E483", {"start": v(112.04, 92.5) * mm, "end": v(112.04, 91.72) * mm});
            skLineSegment(sketch, "E484", {"start": v(112.04, 91.72) * mm, "end": v(111.42, 91.34) * mm});
            skLineSegment(sketch, "E485", {"start": v(111.42, 91.34) * mm, "end": v(111.42, 90.7) * mm});
            skLineSegment(sketch, "E486", {"start": v(111.42, 90.7) * mm, "end": v(110.79, 90.04) * mm});
            skLineSegment(sketch, "E487", {"start": v(110.79, 90.04) * mm, "end": v(110.79, 89.5) * mm});
            skLineSegment(sketch, "E488", {"start": v(110.79, 89.5) * mm, "end": v(110.13, 88.82) * mm});
            skLineSegment(sketch, "E489", {"start": v(110.13, 88.82) * mm, "end": v(110.13, 88.13) * mm});
            skLineSegment(sketch, "E490", {"start": v(110.13, 88.13) * mm, "end": v(109.48, 87.45) * mm});
            skLineSegment(sketch, "E491", {"start": v(109.48, 87.45) * mm, "end": v(109.48, 86.93) * mm});
            skLineSegment(sketch, "E492", {"start": v(109.48, 86.93) * mm, "end": v(108.87, 86.3) * mm});
            skLineSegment(sketch, "E493", {"start": v(108.87, 86.3) * mm, "end": v(108.87, 85.58) * mm});
            skLineSegment(sketch, "E494", {"start": v(108.87, 85.58) * mm, "end": v(108.34, 85.03) * mm});
            skLineSegment(sketch, "E495", {"start": v(108.34, 85.03) * mm, "end": v(108.34, 84.43) * mm});
            skLineSegment(sketch, "E496", {"start": v(108.34, 84.43) * mm, "end": v(107.65, 83.65) * mm});
            skLineSegment(sketch, "E497", {"start": v(107.65, 83.65) * mm, "end": v(107.65, 83.14) * mm});
            skLineSegment(sketch, "E498", {"start": v(107.65, 83.14) * mm, "end": v(107, 82.49) * mm});
            skLineSegment(sketch, "E499", {"start": v(107, 82.49) * mm, "end": v(107, 81.8) * mm});
            skLineSegment(sketch, "E500", {"start": v(107, 81.8) * mm, "end": v(106.38, 81.2) * mm});
            skLineSegment(sketch, "E501", {"start": v(106.38, 81.2) * mm, "end": v(106.38, 80.59) * mm});
            skLineSegment(sketch, "E502", {"start": v(106.38, 80.59) * mm, "end": v(105.77, 79.98) * mm});
            skLineSegment(sketch, "E503", {"start": v(105.77, 79.98) * mm, "end": v(105.77, 79.4) * mm});
            skLineSegment(sketch, "E504", {"start": v(105.77, 79.4) * mm, "end": v(105.1, 78.71) * mm});
            skLineSegment(sketch, "E505", {"start": v(105.1, 78.71) * mm, "end": v(105.1, 77.58) * mm});
            skLineSegment(sketch, "E506", {"start": v(105.1, 77.58) * mm, "end": v(104.56, 77.4) * mm});
            skLineSegment(sketch, "E507", {"start": v(104.56, 77.4) * mm, "end": v(104.56, 76.2) * mm});
            skLineSegment(sketch, "E508", {"start": v(104.56, 76.2) * mm, "end": v(103.86, 75.6) * mm});
            skLineSegment(sketch, "E509", {"start": v(103.86, 75.6) * mm, "end": v(103.86, 74.91) * mm});
            skLineSegment(sketch, "E510", {"start": v(103.86, 74.91) * mm, "end": v(103.3, 74.36) * mm});
            skLineSegment(sketch, "E511", {"start": v(103.3, 74.36) * mm, "end": v(103.27, 73.75) * mm});
            skLineSegment(sketch, "E512", {"start": v(103.27, 73.75) * mm, "end": v(102.64, 73.1) * mm});
            skLineSegment(sketch, "E513", {"start": v(102.64, 73.1) * mm, "end": v(102.64, 72.48) * mm});
            skLineSegment(sketch, "E514", {"start": v(102.64, 72.48) * mm, "end": v(102.05, 71.8) * mm});
            skLineSegment(sketch, "E515", {"start": v(102.05, 71.8) * mm, "end": v(102.05, 71.27) * mm});
            skLineSegment(sketch, "E516", {"start": v(102.05, 71.27) * mm, "end": v(101.48, 70.63) * mm});
            skLineSegment(sketch, "E517", {"start": v(101.48, 70.63) * mm, "end": v(101.48, 70.1) * mm});
            skLineSegment(sketch, "E518", {"start": v(101.48, 70.1) * mm, "end": v(100.74, 69.36) * mm});
            skLineSegment(sketch, "E519", {"start": v(100.74, 69.36) * mm, "end": v(100.74, 68.8) * mm});
            skLineSegment(sketch, "E520", {"start": v(100.74, 68.8) * mm, "end": v(100.11, 68.09) * mm});
            skLineSegment(sketch, "E521", {"start": v(100.11, 68.09) * mm, "end": v(100.11, 67.44) * mm});
            skLineSegment(sketch, "E522", {"start": v(100.11, 67.44) * mm, "end": v(99.49, 66.8) * mm});
            skLineSegment(sketch, "E523", {"start": v(99.49, 66.8) * mm, "end": v(99.49, 66.23) * mm});
            skLineSegment(sketch, "E524", {"start": v(99.49, 66.23) * mm, "end": v(98.88, 65.54) * mm});
            skLineSegment(sketch, "E525", {"start": v(98.88, 65.54) * mm, "end": v(98.88, 65.04) * mm});
            skLineSegment(sketch, "E526", {"start": v(98.88, 65.04) * mm, "end": v(98.22, 64.3) * mm});
            skLineSegment(sketch, "E527", {"start": v(98.22, 64.3) * mm, "end": v(97.6, 63.69) * mm});
            skLineSegment(sketch, "E528", {"start": v(97.6, 63.69) * mm, "end": v(97.6, 63.05) * mm});
            skLineSegment(sketch, "E529", {"start": v(97.6, 63.05) * mm, "end": v(96.96, 62.42) * mm});
            skLineSegment(sketch, "E530", {"start": v(96.96, 62.42) * mm, "end": v(96.96, 61.81) * mm});
            skLineSegment(sketch, "E531", {"start": v(96.96, 61.81) * mm, "end": v(96.33, 61.16) * mm});
            skLineSegment(sketch, "E532", {"start": v(96.33, 61.16) * mm, "end": v(96.33, 60.56) * mm});
            skLineSegment(sketch, "E533", {"start": v(96.33, 60.56) * mm, "end": v(91.3, 55.57) * mm});
            skLineSegment(sketch, "E534", {"start": v(91.3, 55.57) * mm, "end": v(90.67, 55.57) * mm});
            skLineSegment(sketch, "E535", {"start": v(90.67, 55.57) * mm, "end": v(90.1, 54.92) * mm});
            skLineSegment(sketch, "E536", {"start": v(90.1, 54.92) * mm, "end": v(89.47, 54.92) * mm});
            skLineSegment(sketch, "E537", {"start": v(89.47, 54.92) * mm, "end": v(88.88, 54.3) * mm});
            skLineSegment(sketch, "E538", {"start": v(88.88, 54.3) * mm, "end": v(88.24, 54.3) * mm});
            skLineSegment(sketch, "E539", {"start": v(88.24, 54.3) * mm, "end": v(87.58, 53.64) * mm});
            skLineSegment(sketch, "E540", {"start": v(87.58, 53.64) * mm, "end": v(86.3, 53.64) * mm});
            skLineSegment(sketch, "E541", {"start": v(86.3, 53.64) * mm, "end": v(85.7, 53.02) * mm});
            skLineSegment(sketch, "E542", {"start": v(85.7, 53.02) * mm, "end": v(83.82, 53.02) * mm});
            skLineSegment(sketch, "E543", {"start": v(83.82, 53.02) * mm, "end": v(83.22, 52.4) * mm});
            skLineSegment(sketch, "E544", {"start": v(83.22, 52.4) * mm, "end": v(80.66, 52.4) * mm});
            skLineSegment(sketch, "E545", {"start": v(80.66, 52.4) * mm, "end": v(80.03, 51.77) * mm});
            skLineSegment(sketch, "E546", {"start": v(80.03, 51.77) * mm, "end": v(76.28, 51.77) * mm});
            skLineSegment(sketch, "E547", {"start": v(76.28, 51.77) * mm, "end": v(75.64, 51.14) * mm});
            skLineSegment(sketch, "E548", {"start": v(75.64, 51.14) * mm, "end": v(71.84, 51.14) * mm});
            skLineSegment(sketch, "E549", {"start": v(71.84, 51.14) * mm, "end": v(71.3, 50.53) * mm});
            skLineSegment(sketch, "E550", {"start": v(71.3, 50.53) * mm, "end": v(64.2, 50.53) * mm});
            skLineSegment(sketch, "E551", {"start": v(64.2, 50.53) * mm, "end": v(63.66, 49.93) * mm});
            skLineSegment(sketch, "E552", {"start": v(63.66, 49.93) * mm, "end": v(61.86, 49.93) * mm});
            skLineSegment(sketch, "E553", {"start": v(61.86, 49.93) * mm, "end": v(61.22, 49.3) * mm});
            skLineSegment(sketch, "E554", {"start": v(61.22, 49.3) * mm, "end": v(59.96, 49.3) * mm});
            skLineSegment(sketch, "E555", {"start": v(59.96, 49.3) * mm, "end": v(59.33, 48.65) * mm});
            skLineSegment(sketch, "E556", {"start": v(59.33, 48.65) * mm, "end": v(58.66, 48.65) * mm});
            skLineSegment(sketch, "E557", {"start": v(58.66, 48.65) * mm, "end": v(58.05, 47.95) * mm});
            skLineSegment(sketch, "E558", {"start": v(58.05, 47.95) * mm, "end": v(57.47, 47.95) * mm});
            skLineSegment(sketch, "E559", {"start": v(57.47, 47.95) * mm, "end": v(56.8, 47.4) * mm});
            skLineSegment(sketch, "E560", {"start": v(56.8, 47.4) * mm, "end": v(54.94, 47.4) * mm});
            skLineSegment(sketch, "E561", {"start": v(54.94, 47.4) * mm, "end": v(54.26, 46.73) * mm});
            skLineSegment(sketch, "E562", {"start": v(54.26, 46.73) * mm, "end": v(52.45, 46.73) * mm});
            skLineSegment(sketch, "E563", {"start": v(52.45, 46.73) * mm, "end": v(51.84, 46.1) * mm});
            skLineSegment(sketch, "E564", {"start": v(51.84, 46.1) * mm, "end": v(51.3, 46.1) * mm});
            skLineSegment(sketch, "E565", {"start": v(207.2, 172.89) * mm, "end": v(208.07, 172.89) * mm});
            skLineSegment(sketch, "E566", {"start": v(208.07, 172.89) * mm, "end": v(208.63, 173.5) * mm});
            skLineSegment(sketch, "E567", {"start": v(208.63, 173.5) * mm, "end": v(209.25, 173.5) * mm});
            skLineSegment(sketch, "E568", {"start": v(209.25, 173.5) * mm, "end": v(209.9, 174.13) * mm});
            skLineSegment(sketch, "E569", {"start": v(209.9, 174.13) * mm, "end": v(210.57, 174.13) * mm});
            skLineSegment(sketch, "E570", {"start": v(210.57, 174.13) * mm, "end": v(211.74, 175.39) * mm});
            skLineSegment(sketch, "E571", {"start": v(211.74, 175.39) * mm, "end": v(212.39, 175.39) * mm});
            skLineSegment(sketch, "E572", {"start": v(212.39, 175.39) * mm, "end": v(214.3, 177.27) * mm});
            skLineSegment(sketch, "E573", {"start": v(214.3, 177.27) * mm, "end": v(214.94, 177.27) * mm});
            skLineSegment(sketch, "E574", {"start": v(214.94, 177.27) * mm, "end": v(216.24, 178.55) * mm});
            skLineSegment(sketch, "E575", {"start": v(216.24, 178.55) * mm, "end": v(216.82, 178.55) * mm});
            skLineSegment(sketch, "E576", {"start": v(216.82, 178.55) * mm, "end": v(218.7, 180.41) * mm});
            skLineSegment(sketch, "E577", {"start": v(218.7, 180.41) * mm, "end": v(219.59, 180.41) * mm});
            skLineSegment(sketch, "E578", {"start": v(219.59, 180.41) * mm, "end": v(221.2, 181.67) * mm});
            skLineSegment(sketch, "E579", {"start": v(221.2, 181.67) * mm, "end": v(221.85, 182.3) * mm});
            skLineSegment(sketch, "E580", {"start": v(221.85, 182.3) * mm, "end": v(222.48, 182.3) * mm});
            skLineSegment(sketch, "E581", {"start": v(222.48, 182.3) * mm, "end": v(223.1, 182.91) * mm});
            skLineSegment(sketch, "E582", {"start": v(223.1, 182.91) * mm, "end": v(223.73, 182.91) * mm});
            skLineSegment(sketch, "E583", {"start": v(223.73, 182.91) * mm, "end": v(224.37, 183.55) * mm});
            skLineSegment(sketch, "E584", {"start": v(224.37, 183.55) * mm, "end": v(225, 184.16) * mm});
            skLineSegment(sketch, "E585", {"start": v(225, 184.16) * mm, "end": v(225.6, 184.16) * mm});
            skLineSegment(sketch, "E586", {"start": v(225.6, 184.16) * mm, "end": v(226.24, 184.8) * mm});
            skLineSegment(sketch, "E587", {"start": v(226.24, 184.8) * mm, "end": v(226.86, 184.8) * mm});
            skLineSegment(sketch, "E588", {"start": v(226.86, 184.8) * mm, "end": v(227.5, 185.43) * mm});
            skLineSegment(sketch, "E589", {"start": v(227.5, 185.43) * mm, "end": v(228.13, 185.43) * mm});
            skLineSegment(sketch, "E590", {"start": v(228.13, 185.43) * mm, "end": v(229.4, 186.68) * mm});
            skLineSegment(sketch, "E591", {"start": v(229.4, 186.68) * mm, "end": v(230.04, 186.68) * mm});
            skLineSegment(sketch, "E592", {"start": v(230.04, 186.68) * mm, "end": v(231.9, 188.52) * mm});
            skLineSegment(sketch, "E593", {"start": v(231.9, 188.52) * mm, "end": v(232.47, 188.52) * mm});
            skLineSegment(sketch, "E594", {"start": v(232.47, 188.52) * mm, "end": v(233.76, 189.8) * mm});
            skLineSegment(sketch, "E595", {"start": v(233.76, 189.8) * mm, "end": v(234.4, 189.8) * mm});
            skLineSegment(sketch, "E596", {"start": v(234.4, 189.8) * mm, "end": v(235.03, 190.43) * mm});
            skLineSegment(sketch, "E597", {"start": v(235.03, 190.43) * mm, "end": v(235.6, 190.43) * mm});
            skLineSegment(sketch, "E598", {"start": v(235.6, 190.43) * mm, "end": v(236.24, 191.06) * mm});
            skLineSegment(sketch, "E599", {"start": v(236.24, 191.06) * mm, "end": v(236.9, 191.06) * mm});
            skLineSegment(sketch, "E600", {"start": v(236.9, 191.06) * mm, "end": v(237.58, 191.74) * mm});
            skLineSegment(sketch, "E601", {"start": v(237.58, 191.74) * mm, "end": v(238.47, 191.74) * mm});
            skLineSegment(sketch, "E602", {"start": v(238.47, 191.74) * mm, "end": v(238.8, 192.32) * mm});
            skLineSegment(sketch, "E603", {"start": v(238.8, 192.32) * mm, "end": v(239.42, 192.32) * mm});
            skLineSegment(sketch, "E604", {"start": v(239.42, 192.32) * mm, "end": v(240.05, 192.94) * mm});
            skLineSegment(sketch, "E605", {"start": v(240.05, 192.94) * mm, "end": v(240.65, 192.94) * mm});
            skLineSegment(sketch, "E606", {"start": v(240.65, 192.94) * mm, "end": v(241.3, 193.59) * mm});
            skLineSegment(sketch, "E607", {"start": v(241.3, 193.59) * mm, "end": v(241.92, 193.59) * mm});
            skLineSegment(sketch, "E608", {"start": v(241.92, 193.59) * mm, "end": v(242.54, 194.2) * mm});
            skLineSegment(sketch, "E609", {"start": v(242.54, 194.2) * mm, "end": v(243.18, 194.2) * mm});
            skLineSegment(sketch, "E610", {"start": v(243.18, 194.2) * mm, "end": v(243.75, 194.85) * mm});
            skLineSegment(sketch, "E611", {"start": v(243.75, 194.85) * mm, "end": v(244.4, 194.85) * mm});
            skLineSegment(sketch, "E612", {"start": v(244.4, 194.85) * mm, "end": v(245.03, 195.47) * mm});
            skLineSegment(sketch, "E613", {"start": v(245.03, 195.47) * mm, "end": v(245.67, 195.47) * mm});
            skLineSegment(sketch, "E614", {"start": v(245.67, 195.47) * mm, "end": v(246.35, 196.13) * mm});
            skLineSegment(sketch, "E615", {"start": v(246.35, 196.13) * mm, "end": v(246.94, 196.13) * mm});
            skLineSegment(sketch, "E616", {"start": v(246.94, 196.13) * mm, "end": v(247.57, 196.76) * mm});
            skLineSegment(sketch, "E617", {"start": v(247.57, 196.76) * mm, "end": v(248.15, 196.76) * mm});
            skLineSegment(sketch, "E618", {"start": v(248.15, 196.76) * mm, "end": v(248.79, 197.4) * mm});
            skLineSegment(sketch, "E619", {"start": v(248.79, 197.4) * mm, "end": v(249.36, 197.4) * mm});
            skLineSegment(sketch, "E620", {"start": v(249.36, 197.4) * mm, "end": v(250.02, 198.05) * mm});
            skLineSegment(sketch, "E621", {"start": v(250.02, 198.05) * mm, "end": v(251.31, 198.05) * mm});
            skLineSegment(sketch, "E622", {"start": v(251.31, 198.05) * mm, "end": v(251.95, 198.68) * mm});
            skLineSegment(sketch, "E623", {"start": v(251.95, 198.68) * mm, "end": v(252.6, 198.68) * mm});
            skLineSegment(sketch, "E624", {"start": v(252.6, 198.68) * mm, "end": v(253.2, 199.26) * mm});
            skLineSegment(sketch, "E625", {"start": v(253.2, 199.26) * mm, "end": v(253.85, 199.26) * mm});
            skLineSegment(sketch, "E626", {"start": v(253.85, 199.26) * mm, "end": v(254.45, 199.86) * mm});
            skLineSegment(sketch, "E627", {"start": v(254.45, 199.86) * mm, "end": v(255.64, 199.86) * mm});
            skLineSegment(sketch, "E628", {"start": v(255.64, 199.86) * mm, "end": v(256.32, 200.54) * mm});
            skLineSegment(sketch, "E629", {"start": v(256.32, 200.54) * mm, "end": v(256.99, 200.54) * mm});
            skLineSegment(sketch, "E630", {"start": v(256.99, 200.54) * mm, "end": v(257.6, 201.14) * mm});
            skLineSegment(sketch, "E631", {"start": v(257.6, 201.14) * mm, "end": v(258.87, 201.14) * mm});
            skLineSegment(sketch, "E632", {"start": v(258.87, 201.14) * mm, "end": v(259.49, 201.75) * mm});
            skLineSegment(sketch, "E633", {"start": v(259.49, 201.75) * mm, "end": v(260.8, 201.75) * mm});
            skLineSegment(sketch, "E634", {"start": v(260.8, 201.75) * mm, "end": v(261.35, 202.36) * mm});
            skLineSegment(sketch, "E635", {"start": v(261.35, 202.36) * mm, "end": v(262.03, 202.36) * mm});
            skLineSegment(sketch, "E636", {"start": v(262.03, 202.36) * mm, "end": v(262.61, 202.94) * mm});
            skLineSegment(sketch, "E637", {"start": v(262.61, 202.94) * mm, "end": v(263.22, 202.94) * mm});
            skLineSegment(sketch, "E638", {"start": v(263.22, 202.94) * mm, "end": v(263.92, 203.63) * mm});
            skLineSegment(sketch, "E639", {"start": v(263.92, 203.63) * mm, "end": v(265.15, 203.63) * mm});
            skLineSegment(sketch, "E640", {"start": v(265.15, 203.63) * mm, "end": v(265.77, 204.25) * mm});
            skLineSegment(sketch, "E641", {"start": v(265.77, 204.25) * mm, "end": v(266.37, 204.25) * mm});
            skLineSegment(sketch, "E642", {"start": v(266.37, 204.25) * mm, "end": v(267, 204.87) * mm});
            skLineSegment(sketch, "E643", {"start": v(267, 204.87) * mm, "end": v(267.65, 204.87) * mm});
            skLineSegment(sketch, "E644", {"start": v(267.65, 204.87) * mm, "end": v(268.26, 205.54) * mm});
            skLineSegment(sketch, "E645", {"start": v(268.26, 205.54) * mm, "end": v(269.72, 205.54) * mm});
            skLineSegment(sketch, "E646", {"start": v(269.72, 205.54) * mm, "end": v(270.22, 206.1) * mm});
            skLineSegment(sketch, "E647", {"start": v(270.22, 206.1) * mm, "end": v(270.8, 206.1) * mm});
            skLineSegment(sketch, "E648", {"start": v(270.8, 206.1) * mm, "end": v(271.42, 206.79) * mm});
            skLineSegment(sketch, "E649", {"start": v(271.42, 206.79) * mm, "end": v(272.03, 206.79) * mm});
            skLineSegment(sketch, "E650", {"start": v(272.03, 206.79) * mm, "end": v(272.66, 207.4) * mm});
            skLineSegment(sketch, "E651", {"start": v(272.66, 207.4) * mm, "end": v(273.34, 207.4) * mm});
            skLineSegment(sketch, "E652", {"start": v(273.34, 207.4) * mm, "end": v(273.9, 208.03) * mm});
            skLineSegment(sketch, "E653", {"start": v(273.9, 208.03) * mm, "end": v(274.5, 208.03) * mm});
            skLineSegment(sketch, "E654", {"start": v(274.5, 208.03) * mm, "end": v(275.06, 208.65) * mm});
            skLineSegment(sketch, "E655", {"start": v(275.06, 208.65) * mm, "end": v(275.75, 208.65) * mm});
            skLineSegment(sketch, "E656", {"start": v(275.75, 208.65) * mm, "end": v(276.41, 209.3) * mm});
            skLineSegment(sketch, "E657", {"start": v(276.41, 209.3) * mm, "end": v(277, 209.3) * mm});
            skLineSegment(sketch, "E658", {"start": v(277, 209.3) * mm, "end": v(277.64, 209.93) * mm});
            skLineSegment(sketch, "E659", {"start": v(277.64, 209.93) * mm, "end": v(278.3, 209.93) * mm});
            skLineSegment(sketch, "E660", {"start": v(278.3, 209.93) * mm, "end": v(278.96, 210.59) * mm});
            skLineSegment(sketch, "E661", {"start": v(278.96, 210.59) * mm, "end": v(279.53, 210.59) * mm});
            skLineSegment(sketch, "E662", {"start": v(279.53, 210.59) * mm, "end": v(280.1, 211.15) * mm});
            skLineSegment(sketch, "E663", {"start": v(280.1, 211.15) * mm, "end": v(280.8, 211.15) * mm});
            skLineSegment(sketch, "E664", {"start": v(280.8, 211.15) * mm, "end": v(281.42, 211.76) * mm});
            skLineSegment(sketch, "E665", {"start": v(281.42, 211.76) * mm, "end": v(281.95, 211.76) * mm});
            skLineSegment(sketch, "E666", {"start": v(281.95, 211.76) * mm, "end": v(282.55, 212.35) * mm});
            skLineSegment(sketch, "E667", {"start": v(282.55, 212.35) * mm, "end": v(283.35, 212.35) * mm});
            skLineSegment(sketch, "E668", {"start": v(283.35, 212.35) * mm, "end": v(283.96, 213.03) * mm});
            skLineSegment(sketch, "E669", {"start": v(283.96, 213.03) * mm, "end": v(284.59, 213.03) * mm});
            skLineSegment(sketch, "E670", {"start": v(284.59, 213.03) * mm, "end": v(285.2, 213.7) * mm});
            skLineSegment(sketch, "E671", {"start": v(285.2, 213.7) * mm, "end": v(286.23, 213.7) * mm});
            skLineSegment(sketch, "E672", {"start": v(286.23, 213.7) * mm, "end": v(286.93, 214.87) * mm});
            skLineSegment(sketch, "E673", {"start": v(286.93, 214.87) * mm, "end": v(287.68, 214.87) * mm});
            skLineSegment(sketch, "E674", {"start": v(287.68, 214.87) * mm, "end": v(288.39, 215.57) * mm});
            skLineSegment(sketch, "E675", {"start": v(288.39, 215.57) * mm, "end": v(288.98, 215.57) * mm});
            skLineSegment(sketch, "E676", {"start": v(288.98, 215.57) * mm, "end": v(289.57, 216.16) * mm});
            skLineSegment(sketch, "E677", {"start": v(289.57, 216.16) * mm, "end": v(290.2, 216.16) * mm});
            skLineSegment(sketch, "E678", {"start": v(290.2, 216.16) * mm, "end": v(291.38, 217.47) * mm});
            skLineSegment(sketch, "E679", {"start": v(291.38, 217.47) * mm, "end": v(292.05, 217.47) * mm});
            skLineSegment(sketch, "E680", {"start": v(292.05, 217.47) * mm, "end": v(292.76, 218.03) * mm});
            skLineSegment(sketch, "E681", {"start": v(292.76, 218.03) * mm, "end": v(293.4, 218.03) * mm});
            skLineSegment(sketch, "E682", {"start": v(293.4, 218.03) * mm, "end": v(293.87, 218.72) * mm});
            skLineSegment(sketch, "E683", {"start": v(293.87, 218.72) * mm, "end": v(294.67, 218.72) * mm});
            skLineSegment(sketch, "E684", {"start": v(294.67, 218.72) * mm, "end": v(297.21, 221.23) * mm});
            skLineSegment(sketch, "E685", {"start": v(297.21, 221.23) * mm, "end": v(297.74, 221.23) * mm});
            skLineSegment(sketch, "E686", {"start": v(297.74, 221.23) * mm, "end": v(310.5, 233.83) * mm});
            skLineSegment(sketch, "E687", {"start": v(310.5, 233.83) * mm, "end": v(310.5, 234.5) * mm});
            skLineSegment(sketch, "E688", {"start": v(310.5, 234.5) * mm, "end": v(314.12, 238.09) * mm});
            skLineSegment(sketch, "E689", {"start": v(314.12, 238.09) * mm, "end": v(314.12, 238.83) * mm});
            skLineSegment(sketch, "E690", {"start": v(314.12, 238.83) * mm, "end": v(315.95, 240.64) * mm});
            skLineSegment(sketch, "E691", {"start": v(315.95, 240.64) * mm, "end": v(315.95, 241.34) * mm});
            skLineSegment(sketch, "E692", {"start": v(315.95, 241.34) * mm, "end": v(319.07, 244.42) * mm});
            skLineSegment(sketch, "E693", {"start": v(319.07, 244.42) * mm, "end": v(319.07, 245.42) * mm});
            skLineSegment(sketch, "E694", {"start": v(319.07, 245.42) * mm, "end": v(322.2, 248.28) * mm});
            skLineSegment(sketch, "E695", {"start": v(322.2, 248.28) * mm, "end": v(322.2, 248.8) * mm});
            skLineSegment(sketch, "E696", {"start": v(322.2, 248.8) * mm, "end": v(323.5, 250.07) * mm});
            skLineSegment(sketch, "E697", {"start": v(323.5, 250.07) * mm, "end": v(323.5, 250.6) * mm});
            skLineSegment(sketch, "E698", {"start": v(323.5, 250.6) * mm, "end": v(325.45, 252.53) * mm});
            skLineSegment(sketch, "E699", {"start": v(325.45, 252.53) * mm, "end": v(325.45, 253.18) * mm});
            skLineSegment(sketch, "E700", {"start": v(325.45, 253.18) * mm, "end": v(327.29, 255) * mm});
            skLineSegment(sketch, "E701", {"start": v(327.29, 255) * mm, "end": v(327.29, 255.73) * mm});
            skLineSegment(sketch, "E702", {"start": v(327.29, 255.73) * mm, "end": v(329.81, 258.23) * mm});
            skLineSegment(sketch, "E703", {"start": v(329.81, 258.23) * mm, "end": v(329.81, 258.93) * mm});
            skLineSegment(sketch, "E704", {"start": v(329.81, 258.93) * mm, "end": v(331.68, 260.78) * mm});
            skLineSegment(sketch, "E705", {"start": v(331.68, 260.78) * mm, "end": v(331.68, 261.4) * mm});
            skLineSegment(sketch, "E706", {"start": v(331.68, 261.4) * mm, "end": v(332.86, 262.57) * mm});
            skLineSegment(sketch, "E707", {"start": v(332.86, 262.57) * mm, "end": v(332.86, 263.26) * mm});
            skLineSegment(sketch, "E708", {"start": v(332.86, 263.26) * mm, "end": v(334.82, 265.2) * mm});
            skLineSegment(sketch, "E709", {"start": v(334.82, 265.2) * mm, "end": v(334.82, 265.75) * mm});
            skLineSegment(sketch, "E710", {"start": v(334.82, 265.75) * mm, "end": v(336, 267.06) * mm});
            skLineSegment(sketch, "E711", {"start": v(336, 267.06) * mm, "end": v(336, 267.62) * mm});
            skLineSegment(sketch, "E712", {"start": v(336, 267.62) * mm, "end": v(337.3, 268.9) * mm});
            skLineSegment(sketch, "E713", {"start": v(337.3, 268.9) * mm, "end": v(337.3, 269.57) * mm});
            skLineSegment(sketch, "E714", {"start": v(337.3, 269.57) * mm, "end": v(339.15, 271.39) * mm});
            skLineSegment(sketch, "E715", {"start": v(339.15, 271.39) * mm, "end": v(339.15, 272.1) * mm});
            skLineSegment(sketch, "E716", {"start": v(339.15, 272.1) * mm, "end": v(340.38, 273.23) * mm});
            skLineSegment(sketch, "E717", {"start": v(340.38, 273.23) * mm, "end": v(340.38, 273.98) * mm});
            skLineSegment(sketch, "E718", {"start": v(340.38, 273.98) * mm, "end": v(341.05, 274.59) * mm});
            skLineSegment(sketch, "E719", {"start": v(341.05, 274.59) * mm, "end": v(341.05, 275.2) * mm});
            skLineSegment(sketch, "E720", {"start": v(341.05, 275.2) * mm, "end": v(341.72, 275.87) * mm});
            skLineSegment(sketch, "E721", {"start": v(341.72, 275.87) * mm, "end": v(341.72, 276.44) * mm});
            skLineSegment(sketch, "E722", {"start": v(341.72, 276.44) * mm, "end": v(342.96, 277.67) * mm});
            skLineSegment(sketch, "E723", {"start": v(342.96, 277.67) * mm, "end": v(342.95, 278.52) * mm});
            skLineSegment(sketch, "E724", {"start": v(342.95, 278.52) * mm, "end": v(343.4, 279.02) * mm});
            skLineSegment(sketch, "E725", {"start": v(343.4, 279.02) * mm, "end": v(343.4, 279.59) * mm});
            skLineSegment(sketch, "E726", {"start": v(343.4, 279.59) * mm, "end": v(344.82, 280.99) * mm});
            skLineSegment(sketch, "E727", {"start": v(344.82, 280.99) * mm, "end": v(344.82, 281.55) * mm});
            skLineSegment(sketch, "E728", {"start": v(344.82, 281.55) * mm, "end": v(345.4, 282.09) * mm});
            skLineSegment(sketch, "E729", {"start": v(345.4, 282.09) * mm, "end": v(345.4, 282.7) * mm});
            skLineSegment(sketch, "E730", {"start": v(345.4, 282.7) * mm, "end": v(346.08, 283.36) * mm});
            skLineSegment(sketch, "E731", {"start": v(346.08, 283.36) * mm, "end": v(346.08, 283.94) * mm});
            skLineSegment(sketch, "E732", {"start": v(346.08, 283.94) * mm, "end": v(346.76, 284.55) * mm});
            skLineSegment(sketch, "E733", {"start": v(346.76, 284.55) * mm, "end": v(346.76, 285.32) * mm});
            skLineSegment(sketch, "E734", {"start": v(346.76, 285.32) * mm, "end": v(347.35, 285.9) * mm});
            skLineSegment(sketch, "E735", {"start": v(347.35, 285.9) * mm, "end": v(347.35, 286.5) * mm});
            skLineSegment(sketch, "E736", {"start": v(347.35, 286.5) * mm, "end": v(347.94, 287.17) * mm});
            skLineSegment(sketch, "E737", {"start": v(347.94, 287.17) * mm, "end": v(347.94, 287.71) * mm});
            skLineSegment(sketch, "E738", {"start": v(347.94, 287.71) * mm, "end": v(348.66, 288.37) * mm});
            skLineSegment(sketch, "E739", {"start": v(348.66, 288.37) * mm, "end": v(348.66, 288.97) * mm});
            skLineSegment(sketch, "E740", {"start": v(348.66, 288.97) * mm, "end": v(349.22, 289.53) * mm});
            skLineSegment(sketch, "E741", {"start": v(349.22, 289.53) * mm, "end": v(349.22, 290.27) * mm});
            skLineSegment(sketch, "E742", {"start": v(349.22, 290.27) * mm, "end": v(349.84, 290.96) * mm});
            skLineSegment(sketch, "E743", {"start": v(349.84, 290.96) * mm, "end": v(349.84, 291.5) * mm});
            skLineSegment(sketch, "E744", {"start": v(349.84, 291.5) * mm, "end": v(350.53, 292.28) * mm});
            skLineSegment(sketch, "E745", {"start": v(350.53, 292.28) * mm, "end": v(350.53, 292.82) * mm});
            skLineSegment(sketch, "E746", {"start": v(350.53, 292.82) * mm, "end": v(351.06, 293.35) * mm});
            skLineSegment(sketch, "E747", {"start": v(351.06, 293.35) * mm, "end": v(351.06, 293.95) * mm});
            skLineSegment(sketch, "E748", {"start": v(351.06, 293.95) * mm, "end": v(351.7, 294.66) * mm});
            skLineSegment(sketch, "E749", {"start": v(351.7, 294.66) * mm, "end": v(351.7, 295.28) * mm});
            skLineSegment(sketch, "E750", {"start": v(351.7, 295.28) * mm, "end": v(352.28, 295.92) * mm});
            skLineSegment(sketch, "E751", {"start": v(352.28, 295.92) * mm, "end": v(352.3, 296.46) * mm});
            skLineSegment(sketch, "E752", {"start": v(352.3, 296.46) * mm, "end": v(352.98, 297.08) * mm});
            skLineSegment(sketch, "E753", {"start": v(352.98, 297.08) * mm, "end": v(352.98, 297.87) * mm});
            skLineSegment(sketch, "E754", {"start": v(352.98, 297.87) * mm, "end": v(353.6, 298.48) * mm});
            skLineSegment(sketch, "E755", {"start": v(353.6, 298.48) * mm, "end": v(353.6, 299) * mm});
            skLineSegment(sketch, "E756", {"start": v(353.6, 299) * mm, "end": v(354.3, 299.44) * mm});
            skLineSegment(sketch, "E757", {"start": v(354.3, 299.44) * mm, "end": v(354.3, 300.34) * mm});
            skLineSegment(sketch, "E758", {"start": v(354.3, 300.34) * mm, "end": v(354.89, 301) * mm});
            skLineSegment(sketch, "E759", {"start": v(354.89, 301) * mm, "end": v(354.89, 302.13) * mm});
            skLineSegment(sketch, "E760", {"start": v(354.89, 302.13) * mm, "end": v(355.44, 302.75) * mm});
            skLineSegment(sketch, "E761", {"start": v(355.44, 302.75) * mm, "end": v(355.44, 303.55) * mm});
            skLineSegment(sketch, "E762", {"start": v(355.44, 303.55) * mm, "end": v(356, 304.1) * mm});
            skLineSegment(sketch, "E763", {"start": v(356, 304.1) * mm, "end": v(356, 304.7) * mm});
            skLineSegment(sketch, "E764", {"start": v(356, 304.7) * mm, "end": v(356.64, 305.4) * mm});
            skLineSegment(sketch, "E765", {"start": v(356.64, 305.4) * mm, "end": v(356.64, 306.05) * mm});
            skLineSegment(sketch, "E766", {"start": v(356.64, 306.05) * mm, "end": v(357.32, 306.72) * mm});
            skLineSegment(sketch, "E767", {"start": v(357.32, 306.72) * mm, "end": v(357.32, 307.72) * mm});
            skLineSegment(sketch, "E768", {"start": v(357.32, 307.72) * mm, "end": v(358.03, 308.4) * mm});
            skLineSegment(sketch, "E769", {"start": v(358.03, 308.4) * mm, "end": v(358.03, 309.12) * mm});
            skLineSegment(sketch, "E770", {"start": v(358.03, 309.12) * mm, "end": v(358.68, 309.53) * mm});
            skLineSegment(sketch, "E771", {"start": v(358.68, 309.53) * mm, "end": v(358.68, 310.36) * mm});
            skLineSegment(sketch, "E772", {"start": v(358.68, 310.36) * mm, "end": v(359.21, 310.95) * mm});
            skLineSegment(sketch, "E773", {"start": v(359.21, 310.95) * mm, "end": v(359.21, 311.55) * mm});
            skLineSegment(sketch, "E774", {"start": v(359.21, 311.55) * mm, "end": v(359.85, 312.26) * mm});
            skLineSegment(sketch, "E775", {"start": v(359.85, 312.26) * mm, "end": v(359.85, 312.84) * mm});
            skLineSegment(sketch, "E776", {"start": v(359.85, 312.84) * mm, "end": v(360.55, 313.28) * mm});
            skLineSegment(sketch, "E777", {"start": v(360.55, 313.28) * mm, "end": v(360.55, 314.17) * mm});
            skLineSegment(sketch, "E778", {"start": v(360.55, 314.17) * mm, "end": v(361.15, 314.76) * mm});
            skLineSegment(sketch, "E779", {"start": v(361.15, 314.76) * mm, "end": v(361.15, 315.4) * mm});
            skLineSegment(sketch, "E780", {"start": v(361.15, 315.4) * mm, "end": v(361.82, 316.08) * mm});
            skLineSegment(sketch, "E781", {"start": v(361.82, 316.08) * mm, "end": v(361.82, 316.8) * mm});
            skLineSegment(sketch, "E782", {"start": v(361.82, 316.8) * mm, "end": v(362.4, 317.81) * mm});
            skLineSegment(sketch, "E783", {"start": v(362.4, 317.81) * mm, "end": v(363.67, 319.06) * mm});
            skLineSegment(sketch, "E784", {"start": v(363.67, 319.06) * mm, "end": v(363.67, 319.8) * mm});
            skLineSegment(sketch, "E785", {"start": v(363.67, 319.8) * mm, "end": v(364.26, 320.38) * mm});
            skLineSegment(sketch, "E786", {"start": v(364.26, 320.38) * mm, "end": v(364.26, 321.03) * mm});
            skLineSegment(sketch, "E787", {"start": v(364.26, 321.03) * mm, "end": v(365.53, 322.29) * mm});
            skLineSegment(sketch, "E788", {"start": v(365.53, 322.29) * mm, "end": v(365.53, 322.83) * mm});
            skLineSegment(sketch, "E789", {"start": v(365.53, 322.83) * mm, "end": v(368.1, 325.37) * mm});
            skLineSegment(sketch, "E790", {"start": v(368.1, 325.37) * mm, "end": v(368.65, 325.37) * mm});
            skLineSegment(sketch, "E791", {"start": v(368.65, 325.37) * mm, "end": v(370.57, 327.27) * mm});
            skLineSegment(sketch, "E792", {"start": v(370.57, 327.27) * mm, "end": v(372.47, 327.27) * mm});
            skLineSegment(sketch, "E793", {"start": v(372.47, 327.27) * mm, "end": v(373.07, 326.67) * mm});
            skLineSegment(sketch, "E794", {"start": v(373.07, 326.67) * mm, "end": v(374.92, 326.67) * mm});
            skLineSegment(sketch, "E795", {"start": v(374.92, 326.67) * mm, "end": v(376.97, 324.83) * mm});
            skLineSegment(sketch, "E796", {"start": v(376.97, 324.83) * mm, "end": v(376.97, 324.13) * mm});
            skLineSegment(sketch, "E797", {"start": v(376.97, 324.13) * mm, "end": v(379.35, 321.72) * mm});
            skLineSegment(sketch, "E798", {"start": v(379.35, 321.72) * mm, "end": v(379.35, 320.71) * mm});
            skLineSegment(sketch, "E799", {"start": v(379.35, 320.71) * mm, "end": v(379.97, 320.35) * mm});
            skLineSegment(sketch, "E800", {"start": v(379.97, 320.35) * mm, "end": v(379.97, 319.6) * mm});
            skLineSegment(sketch, "E801", {"start": v(379.97, 319.6) * mm, "end": v(380.61, 319.03) * mm});
            skLineSegment(sketch, "E802", {"start": v(380.61, 319.03) * mm, "end": v(380.61, 318.45) * mm});
            skLineSegment(sketch, "E803", {"start": v(380.61, 318.45) * mm, "end": v(381.22, 317.85) * mm});
            skLineSegment(sketch, "E804", {"start": v(381.22, 317.85) * mm, "end": v(381.22, 317.17) * mm});
            skLineSegment(sketch, "E805", {"start": v(381.22, 317.17) * mm, "end": v(381.87, 316.58) * mm});
            skLineSegment(sketch, "E806", {"start": v(381.87, 316.58) * mm, "end": v(381.87, 316) * mm});
            skLineSegment(sketch, "E807", {"start": v(381.87, 316) * mm, "end": v(382.49, 315.38) * mm});
            skLineSegment(sketch, "E808", {"start": v(382.49, 315.38) * mm, "end": v(382.49, 314.73) * mm});
            skLineSegment(sketch, "E809", {"start": v(382.49, 314.73) * mm, "end": v(383.11, 314.1) * mm});
            skLineSegment(sketch, "E810", {"start": v(383.11, 314.1) * mm, "end": v(383.11, 313.45) * mm});
            skLineSegment(sketch, "E811", {"start": v(383.11, 313.45) * mm, "end": v(383.7, 312.86) * mm});
            skLineSegment(sketch, "E812", {"start": v(383.7, 312.86) * mm, "end": v(383.7, 312.23) * mm});
            skLineSegment(sketch, "E813", {"start": v(383.7, 312.23) * mm, "end": v(384.4, 311.55) * mm});
            skLineSegment(sketch, "E814", {"start": v(384.4, 311.55) * mm, "end": v(384.4, 310.96) * mm});
            skLineSegment(sketch, "E815", {"start": v(384.4, 310.96) * mm, "end": v(385.03, 310.35) * mm});
            skLineSegment(sketch, "E816", {"start": v(385.03, 310.35) * mm, "end": v(385.03, 309.12) * mm});
            skLineSegment(sketch, "E817", {"start": v(385.03, 309.12) * mm, "end": v(385.65, 308.45) * mm});
            skLineSegment(sketch, "E818", {"start": v(385.65, 308.45) * mm, "end": v(385.65, 307.85) * mm});
            skLineSegment(sketch, "E819", {"start": v(385.65, 307.85) * mm, "end": v(386.29, 307.24) * mm});
            skLineSegment(sketch, "E820", {"start": v(386.29, 307.24) * mm, "end": v(386.29, 306.41) * mm});
            skLineSegment(sketch, "E821", {"start": v(386.29, 306.41) * mm, "end": v(386.88, 305.79) * mm});
            skLineSegment(sketch, "E822", {"start": v(386.88, 305.79) * mm, "end": v(386.88, 304.7) * mm});
            skLineSegment(sketch, "E823", {"start": v(386.88, 304.7) * mm, "end": v(387.52, 304.06) * mm});
            skLineSegment(sketch, "E824", {"start": v(387.52, 304.06) * mm, "end": v(387.52, 303.38) * mm});
            skLineSegment(sketch, "E825", {"start": v(387.52, 303.38) * mm, "end": v(388.2, 302.74) * mm});
            skLineSegment(sketch, "E826", {"start": v(388.2, 302.74) * mm, "end": v(388.2, 301.47) * mm});
            skLineSegment(sketch, "E827", {"start": v(388.2, 301.47) * mm, "end": v(388.82, 300.9) * mm});
            skLineSegment(sketch, "E828", {"start": v(388.82, 300.9) * mm, "end": v(388.82, 299.78) * mm});
            skLineSegment(sketch, "E829", {"start": v(388.82, 299.78) * mm, "end": v(389.43, 299.11) * mm});
            skLineSegment(sketch, "E830", {"start": v(389.43, 299.11) * mm, "end": v(389.43, 297.67) * mm});
            skLineSegment(sketch, "E831", {"start": v(389.43, 297.67) * mm, "end": v(389.99, 297.16) * mm});
            skLineSegment(sketch, "E832", {"start": v(389.99, 297.16) * mm, "end": v(389.99, 295.4) * mm});
            skLineSegment(sketch, "E833", {"start": v(389.99, 295.4) * mm, "end": v(390.72, 294.74) * mm});
            skLineSegment(sketch, "E834", {"start": v(390.72, 294.74) * mm, "end": v(390.72, 293.2) * mm});
            skLineSegment(sketch, "E835", {"start": v(390.72, 293.2) * mm, "end": v(391.25, 292.73) * mm});
            skLineSegment(sketch, "E836", {"start": v(391.25, 292.73) * mm, "end": v(391.25, 291.4) * mm});
            skLineSegment(sketch, "E837", {"start": v(391.25, 291.4) * mm, "end": v(392, 290.73) * mm});
            skLineSegment(sketch, "E838", {"start": v(392, 290.73) * mm, "end": v(392, 289.4) * mm});
            skLineSegment(sketch, "E839", {"start": v(392, 289.4) * mm, "end": v(392.64, 288.92) * mm});
            skLineSegment(sketch, "E840", {"start": v(392.64, 288.92) * mm, "end": v(392.64, 287.75) * mm});
            skLineSegment(sketch, "E841", {"start": v(392.64, 287.75) * mm, "end": v(393.22, 287.17) * mm});
            skLineSegment(sketch, "E842", {"start": v(393.22, 287.17) * mm, "end": v(393.22, 285.22) * mm});
            skLineSegment(sketch, "E843", {"start": v(393.22, 285.22) * mm, "end": v(393.88, 284.63) * mm});
            skLineSegment(sketch, "E844", {"start": v(393.88, 284.63) * mm, "end": v(393.88, 282.7) * mm});
            skLineSegment(sketch, "E845", {"start": v(393.88, 282.7) * mm, "end": v(394.5, 282.14) * mm});
            skLineSegment(sketch, "E846", {"start": v(394.5, 282.14) * mm, "end": v(394.5, 280.67) * mm});
            skLineSegment(sketch, "E847", {"start": v(394.5, 280.67) * mm, "end": v(395.1, 280.13) * mm});
            skLineSegment(sketch, "E848", {"start": v(395.1, 280.13) * mm, "end": v(395.1, 278.29) * mm});
            skLineSegment(sketch, "E849", {"start": v(395.1, 278.29) * mm, "end": v(395.75, 277.7) * mm});
            skLineSegment(sketch, "E850", {"start": v(395.75, 277.7) * mm, "end": v(395.75, 276.15) * mm});
            skLineSegment(sketch, "E851", {"start": v(395.75, 276.15) * mm, "end": v(396.29, 275.66) * mm});
            skLineSegment(sketch, "E852", {"start": v(396.29, 275.66) * mm, "end": v(396.29, 273.86) * mm});
            skLineSegment(sketch, "E853", {"start": v(396.29, 273.86) * mm, "end": v(396.94, 273.09) * mm});
            skLineSegment(sketch, "E854", {"start": v(396.94, 273.09) * mm, "end": v(396.94, 271.35) * mm});
            skLineSegment(sketch, "E855", {"start": v(396.94, 271.35) * mm, "end": v(397.56, 270.85) * mm});
            skLineSegment(sketch, "E856", {"start": v(397.56, 270.85) * mm, "end": v(397.56, 268.97) * mm});
            skLineSegment(sketch, "E857", {"start": v(397.56, 268.97) * mm, "end": v(398.22, 268.24) * mm});
            skLineSegment(sketch, "E858", {"start": v(398.22, 268.24) * mm, "end": v(398.22, 265.84) * mm});
            skLineSegment(sketch, "E859", {"start": v(398.22, 265.84) * mm, "end": v(398.82, 265.3) * mm});
            skLineSegment(sketch, "E860", {"start": v(398.82, 265.3) * mm, "end": v(398.82, 262.03) * mm});
            skLineSegment(sketch, "E861", {"start": v(398.82, 262.03) * mm, "end": v(399.42, 261.37) * mm});
            skLineSegment(sketch, "E862", {"start": v(399.42, 261.37) * mm, "end": v(399.42, 258.82) * mm});
            skLineSegment(sketch, "E863", {"start": v(399.42, 258.82) * mm, "end": v(399.98, 258.33) * mm});
            skLineSegment(sketch, "E864", {"start": v(399.98, 258.33) * mm, "end": v(399.98, 255.77) * mm});
            skLineSegment(sketch, "E865", {"start": v(399.98, 255.77) * mm, "end": v(400.7, 255.17) * mm});
            skLineSegment(sketch, "E866", {"start": v(400.7, 255.17) * mm, "end": v(400.7, 251.93) * mm});
            skLineSegment(sketch, "E867", {"start": v(400.7, 251.93) * mm, "end": v(401.4, 251.35) * mm});
            skLineSegment(sketch, "E868", {"start": v(401.4, 251.35) * mm, "end": v(401.4, 249) * mm});
            skLineSegment(sketch, "E869", {"start": v(401.4, 249) * mm, "end": v(402.01, 248.32) * mm});
            skLineSegment(sketch, "E870", {"start": v(402.01, 248.32) * mm, "end": v(402.01, 245.08) * mm});
            skLineSegment(sketch, "E871", {"start": v(402.01, 245.08) * mm, "end": v(402.6, 244.4) * mm});
            skLineSegment(sketch, "E872", {"start": v(402.6, 244.4) * mm, "end": v(402.6, 241.34) * mm});
            skLineSegment(sketch, "E873", {"start": v(402.6, 241.34) * mm, "end": v(403.28, 240.56) * mm});
            skLineSegment(sketch, "E874", {"start": v(403.28, 240.56) * mm, "end": v(403.28, 236.84) * mm});
            skLineSegment(sketch, "E875", {"start": v(403.28, 236.84) * mm, "end": v(403.84, 236.3) * mm});
            skLineSegment(sketch, "E876", {"start": v(403.84, 236.3) * mm, "end": v(403.84, 233.1) * mm});
            skLineSegment(sketch, "E877", {"start": v(403.84, 233.1) * mm, "end": v(404.41, 232.53) * mm});
            skLineSegment(sketch, "E878", {"start": v(404.41, 232.53) * mm, "end": v(404.41, 229.34) * mm});
            skLineSegment(sketch, "E879", {"start": v(404.41, 229.34) * mm, "end": v(405.07, 228.65) * mm});
            skLineSegment(sketch, "E880", {"start": v(405.07, 228.65) * mm, "end": v(405.07, 225.02) * mm});
            skLineSegment(sketch, "E881", {"start": v(405.07, 225.02) * mm, "end": v(405.74, 224.32) * mm});
            skLineSegment(sketch, "E882", {"start": v(405.74, 224.32) * mm, "end": v(405.74, 221.22) * mm});
            skLineSegment(sketch, "E883", {"start": v(405.74, 221.22) * mm, "end": v(406.32, 220.7) * mm});
            skLineSegment(sketch, "E884", {"start": v(406.32, 220.7) * mm, "end": v(406.32, 216.96) * mm});
            skLineSegment(sketch, "E885", {"start": v(406.32, 216.96) * mm, "end": v(406.97, 216.12) * mm});
            skLineSegment(sketch, "E886", {"start": v(406.97, 216.12) * mm, "end": v(406.97, 213.13) * mm});
            skLineSegment(sketch, "E887", {"start": v(406.97, 213.13) * mm, "end": v(407.57, 212.3) * mm});
            skLineSegment(sketch, "E888", {"start": v(407.57, 212.3) * mm, "end": v(407.58, 208.67) * mm});
            skLineSegment(sketch, "E889", {"start": v(407.58, 208.67) * mm, "end": v(408.2, 208.11) * mm});
            skLineSegment(sketch, "E890", {"start": v(408.2, 208.11) * mm, "end": v(408.2, 204.14) * mm});
            skLineSegment(sketch, "E891", {"start": v(408.2, 204.14) * mm, "end": v(408.9, 203.5) * mm});
            skLineSegment(sketch, "E892", {"start": v(408.9, 203.5) * mm, "end": v(408.9, 200.4) * mm});
            skLineSegment(sketch, "E893", {"start": v(408.9, 200.4) * mm, "end": v(409.48, 199.8) * mm});
            skLineSegment(sketch, "E894", {"start": v(409.48, 199.8) * mm, "end": v(409.48, 196.1) * mm});
            skLineSegment(sketch, "E895", {"start": v(409.48, 196.1) * mm, "end": v(410.14, 195.33) * mm});
            skLineSegment(sketch, "E896", {"start": v(410.14, 195.33) * mm, "end": v(410.15, 192.4) * mm});
            skLineSegment(sketch, "E897", {"start": v(410.15, 192.4) * mm, "end": v(410.76, 191.74) * mm});
            skLineSegment(sketch, "E898", {"start": v(410.76, 191.74) * mm, "end": v(410.76, 188.55) * mm});
            skLineSegment(sketch, "E899", {"start": v(410.76, 188.55) * mm, "end": v(411.36, 188) * mm});
            skLineSegment(sketch, "E900", {"start": v(411.36, 188) * mm, "end": v(411.36, 184.74) * mm});
            skLineSegment(sketch, "E901", {"start": v(411.36, 184.74) * mm, "end": v(411.97, 184.24) * mm});
            skLineSegment(sketch, "E902", {"start": v(411.97, 184.24) * mm, "end": v(411.97, 181.12) * mm});
            skLineSegment(sketch, "E903", {"start": v(411.97, 181.12) * mm, "end": v(412.78, 180.4) * mm});
            skLineSegment(sketch, "E904", {"start": v(412.78, 180.4) * mm, "end": v(412.78, 177.25) * mm});
            skLineSegment(sketch, "E905", {"start": v(412.78, 177.25) * mm, "end": v(413.22, 176.6) * mm});
            skLineSegment(sketch, "E906", {"start": v(413.22, 176.6) * mm, "end": v(413.22, 174.13) * mm});
            skLineSegment(sketch, "E907", {"start": v(413.22, 174.13) * mm, "end": v(413.81, 173.5) * mm});
            skLineSegment(sketch, "E908", {"start": v(413.81, 173.5) * mm, "end": v(413.81, 170.43) * mm});
            skLineSegment(sketch, "E909", {"start": v(413.81, 170.43) * mm, "end": v(414.52, 169.7) * mm});
            skLineSegment(sketch, "E910", {"start": v(414.52, 169.7) * mm, "end": v(414.52, 166.9) * mm});
            skLineSegment(sketch, "E911", {"start": v(414.52, 166.9) * mm, "end": v(415.15, 166.2) * mm});
            skLineSegment(sketch, "E912", {"start": v(415.15, 166.2) * mm, "end": v(415.15, 163.4) * mm});
            skLineSegment(sketch, "E913", {"start": v(415.15, 163.4) * mm, "end": v(415.76, 162.73) * mm});
            skLineSegment(sketch, "E914", {"start": v(415.76, 162.73) * mm, "end": v(415.76, 161.07) * mm});
            skLineSegment(sketch, "E915", {"start": v(415.76, 161.07) * mm, "end": v(416.41, 160.37) * mm});
            skLineSegment(sketch, "E916", {"start": v(416.41, 160.37) * mm, "end": v(416.41, 158.43) * mm});
            skLineSegment(sketch, "E917", {"start": v(416.41, 158.43) * mm, "end": v(417.12, 157.6) * mm});
            skLineSegment(sketch, "E918", {"start": v(417.12, 157.6) * mm, "end": v(417.12, 156) * mm});
            skLineSegment(sketch, "E919", {"start": v(417.12, 156) * mm, "end": v(417.7, 155.47) * mm});
            skLineSegment(sketch, "E920", {"start": v(417.7, 155.47) * mm, "end": v(417.7, 153.52) * mm});
            skLineSegment(sketch, "E921", {"start": v(417.7, 153.52) * mm, "end": v(418.33, 152.91) * mm});
            skLineSegment(sketch, "E922", {"start": v(418.33, 152.91) * mm, "end": v(418.33, 150.62) * mm});
            skLineSegment(sketch, "E923", {"start": v(418.33, 150.62) * mm, "end": v(418.9, 150.1) * mm});
            skLineSegment(sketch, "E924", {"start": v(418.9, 150.1) * mm, "end": v(418.9, 148.47) * mm});
            skLineSegment(sketch, "E925", {"start": v(418.9, 148.47) * mm, "end": v(419.56, 147.88) * mm});
            skLineSegment(sketch, "E926", {"start": v(419.56, 147.88) * mm, "end": v(419.56, 146.2) * mm});
            skLineSegment(sketch, "E927", {"start": v(419.56, 146.2) * mm, "end": v(420.16, 145.89) * mm});
            skLineSegment(sketch, "E928", {"start": v(420.16, 145.89) * mm, "end": v(420.16, 145.13) * mm});
            skLineSegment(sketch, "E929", {"start": v(420.16, 145.13) * mm, "end": v(420.69, 144.66) * mm});
            skLineSegment(sketch, "E930", {"start": v(420.69, 144.66) * mm, "end": v(420.69, 143.37) * mm});
            skLineSegment(sketch, "E931", {"start": v(420.69, 143.37) * mm, "end": v(421.42, 142.75) * mm});
            skLineSegment(sketch, "E932", {"start": v(421.42, 142.75) * mm, "end": v(421.4, 142.14) * mm});
            skLineSegment(sketch, "E933", {"start": v(421.4, 142.14) * mm, "end": v(421.98, 141.5) * mm});
            skLineSegment(sketch, "E934", {"start": v(421.98, 141.5) * mm, "end": v(421.96, 140.96) * mm});
            skLineSegment(sketch, "E935", {"start": v(421.96, 140.96) * mm, "end": v(422.65, 140.34) * mm});
            skLineSegment(sketch, "E936", {"start": v(422.65, 140.34) * mm, "end": v(422.66, 138.95) * mm});
            skLineSegment(sketch, "E937", {"start": v(422.66, 138.95) * mm, "end": v(423.3, 138.37) * mm});
            skLineSegment(sketch, "E938", {"start": v(423.3, 138.37) * mm, "end": v(423.3, 137.79) * mm});
            skLineSegment(sketch, "E939", {"start": v(423.3, 137.79) * mm, "end": v(423.91, 137.2) * mm});
            skLineSegment(sketch, "E940", {"start": v(423.91, 137.2) * mm, "end": v(423.91, 136.14) * mm});
            skLineSegment(sketch, "E941", {"start": v(423.91, 136.14) * mm, "end": v(424.56, 135.9) * mm});
            skLineSegment(sketch, "E942", {"start": v(424.56, 135.9) * mm, "end": v(424.56, 135.16) * mm});
            skLineSegment(sketch, "E943", {"start": v(424.56, 135.16) * mm, "end": v(425.18, 134.58) * mm});
            skLineSegment(sketch, "E944", {"start": v(425.18, 134.58) * mm, "end": v(425.18, 134) * mm});
            skLineSegment(sketch, "E945", {"start": v(425.18, 134) * mm, "end": v(425.75, 133.34) * mm});
            skLineSegment(sketch, "E946", {"start": v(425.75, 133.34) * mm, "end": v(425.75, 132.81) * mm});
            skLineSegment(sketch, "E947", {"start": v(425.75, 132.81) * mm, "end": v(426.44, 132.1) * mm});
            skLineSegment(sketch, "E948", {"start": v(426.44, 132.1) * mm, "end": v(426.44, 131.5) * mm});
            skLineSegment(sketch, "E949", {"start": v(426.44, 131.5) * mm, "end": v(427, 130.96) * mm});
            skLineSegment(sketch, "E950", {"start": v(427, 130.96) * mm, "end": v(427.02, 130.3) * mm});
            skLineSegment(sketch, "E951", {"start": v(427.02, 130.3) * mm, "end": v(427.65, 129.55) * mm});
            skLineSegment(sketch, "E952", {"start": v(427.65, 129.55) * mm, "end": v(427.65, 128.94) * mm});
            skLineSegment(sketch, "E953", {"start": v(427.65, 128.94) * mm, "end": v(428.34, 128.59) * mm});
            skLineSegment(sketch, "E954", {"start": v(428.34, 128.59) * mm, "end": v(428.33, 128.02) * mm});
            skLineSegment(sketch, "E955", {"start": v(428.33, 128.02) * mm, "end": v(428.9, 127.68) * mm});
            skLineSegment(sketch, "E956", {"start": v(428.9, 127.68) * mm, "end": v(428.93, 127.06) * mm});
            skLineSegment(sketch, "E957", {"start": v(428.93, 127.06) * mm, "end": v(429.6, 126.43) * mm});
            skLineSegment(sketch, "E958", {"start": v(429.6, 126.43) * mm, "end": v(429.6, 125.86) * mm});
            skLineSegment(sketch, "E959", {"start": v(429.6, 125.86) * mm, "end": v(430.17, 125.18) * mm});
            skLineSegment(sketch, "E960", {"start": v(430.17, 125.18) * mm, "end": v(430.17, 124.57) * mm});
            skLineSegment(sketch, "E961", {"start": v(430.17, 124.57) * mm, "end": v(430.82, 124) * mm});
            skLineSegment(sketch, "E962", {"start": v(430.82, 124) * mm, "end": v(430.82, 123.3) * mm});
            skLineSegment(sketch, "E963", {"start": v(430.82, 123.3) * mm, "end": v(431.47, 122.67) * mm});
            skLineSegment(sketch, "E964", {"start": v(431.47, 122.67) * mm, "end": v(431.47, 121.83) * mm});
            skLineSegment(sketch, "E965", {"start": v(431.47, 121.83) * mm, "end": v(432.09, 121.43) * mm});
            skLineSegment(sketch, "E966", {"start": v(432.09, 121.43) * mm, "end": v(432.09, 120.88) * mm});
            skLineSegment(sketch, "E967", {"start": v(432.09, 120.88) * mm, "end": v(432.7, 120.33) * mm});
            skLineSegment(sketch, "E968", {"start": v(432.7, 120.33) * mm, "end": v(432.72, 119.5) * mm});
            skLineSegment(sketch, "E969", {"start": v(432.72, 119.5) * mm, "end": v(433.34, 118.95) * mm});
            skLineSegment(sketch, "E970", {"start": v(433.34, 118.95) * mm, "end": v(433.34, 118.26) * mm});
            skLineSegment(sketch, "E971", {"start": v(433.34, 118.26) * mm, "end": v(433.98, 117.67) * mm});
            skLineSegment(sketch, "E972", {"start": v(433.98, 117.67) * mm, "end": v(433.98, 117.04) * mm});
            skLineSegment(sketch, "E973", {"start": v(433.98, 117.04) * mm, "end": v(434.62, 116.43) * mm});
            skLineSegment(sketch, "E974", {"start": v(434.62, 116.43) * mm, "end": v(434.62, 115.83) * mm});
            skLineSegment(sketch, "E975", {"start": v(434.62, 115.83) * mm, "end": v(435.23, 115.25) * mm});
            skLineSegment(sketch, "E976", {"start": v(435.23, 115.25) * mm, "end": v(435.23, 114.6) * mm});
            skLineSegment(sketch, "E977", {"start": v(435.23, 114.6) * mm, "end": v(435.78, 114.1) * mm});
            skLineSegment(sketch, "E978", {"start": v(435.78, 114.1) * mm, "end": v(435.78, 113.32) * mm});
            skLineSegment(sketch, "E979", {"start": v(435.78, 113.32) * mm, "end": v(436.45, 112.59) * mm});
            skLineSegment(sketch, "E980", {"start": v(436.45, 112.59) * mm, "end": v(436.45, 111.9) * mm});
            skLineSegment(sketch, "E981", {"start": v(436.45, 111.9) * mm, "end": v(437.16, 111.3) * mm});
            skLineSegment(sketch, "E982", {"start": v(437.16, 111.3) * mm, "end": v(437.16, 109.92) * mm});
            skLineSegment(sketch, "E983", {"start": v(437.16, 109.92) * mm, "end": v(437.69, 109.61) * mm});
            skLineSegment(sketch, "E984", {"start": v(437.69, 109.61) * mm, "end": v(437.69, 108.88) * mm});
            skLineSegment(sketch, "E985", {"start": v(437.69, 108.88) * mm, "end": v(438.35, 108.33) * mm});
            skLineSegment(sketch, "E986", {"start": v(438.35, 108.33) * mm, "end": v(438.36, 107.65) * mm});
            skLineSegment(sketch, "E987", {"start": v(438.36, 107.65) * mm, "end": v(438.97, 107.08) * mm});
            skLineSegment(sketch, "E988", {"start": v(438.97, 107.08) * mm, "end": v(438.97, 105.78) * mm});
            skLineSegment(sketch, "E989", {"start": v(438.97, 105.78) * mm, "end": v(439.66, 105.14) * mm});
            skLineSegment(sketch, "E990", {"start": v(439.66, 105.14) * mm, "end": v(439.66, 104.42) * mm});
            skLineSegment(sketch, "E991", {"start": v(439.66, 104.42) * mm, "end": v(440.24, 103.92) * mm});
            skLineSegment(sketch, "E992", {"start": v(440.24, 103.92) * mm, "end": v(440.24, 103.18) * mm});
            skLineSegment(sketch, "E993", {"start": v(440.24, 103.18) * mm, "end": v(440.93, 102.53) * mm});
            skLineSegment(sketch, "E994", {"start": v(440.93, 102.53) * mm, "end": v(440.96, 101.92) * mm});
            skLineSegment(sketch, "E995", {"start": v(440.96, 101.92) * mm, "end": v(441.5, 101.34) * mm});
            skLineSegment(sketch, "E996", {"start": v(441.5, 101.34) * mm, "end": v(441.5, 99.98) * mm});
            skLineSegment(sketch, "E997", {"start": v(441.5, 99.98) * mm, "end": v(442.08, 99.47) * mm});
            skLineSegment(sketch, "E998", {"start": v(442.08, 99.47) * mm, "end": v(442.09, 98.83) * mm});
            skLineSegment(sketch, "E999", {"start": v(442.09, 98.83) * mm, "end": v(442.73, 98.26) * mm});
            skLineSegment(sketch, "E1000", {"start": v(442.73, 98.26) * mm, "end": v(442.73, 97.62) * mm});
            skLineSegment(sketch, "E1001", {"start": v(442.73, 97.62) * mm, "end": v(443.36, 96.98) * mm});
            skLineSegment(sketch, "E1002", {"start": v(443.36, 96.98) * mm, "end": v(443.36, 95.75) * mm});
            skLineSegment(sketch, "E1003", {"start": v(443.36, 95.75) * mm, "end": v(444.03, 95.07) * mm});
            skLineSegment(sketch, "E1004", {"start": v(444.03, 95.07) * mm, "end": v(444.02, 94.39) * mm});
            skLineSegment(sketch, "E1005", {"start": v(444.02, 94.39) * mm, "end": v(444.57, 93.89) * mm});
            skLineSegment(sketch, "E1006", {"start": v(444.57, 93.89) * mm, "end": v(444.57, 93.25) * mm});
            skLineSegment(sketch, "E1007", {"start": v(444.57, 93.25) * mm, "end": v(445.25, 92.6) * mm});
            skLineSegment(sketch, "E1008", {"start": v(445.25, 92.6) * mm, "end": v(445.25, 91.68) * mm});
            skLineSegment(sketch, "E1009", {"start": v(445.25, 91.68) * mm, "end": v(445.86, 91.27) * mm});
            skLineSegment(sketch, "E1010", {"start": v(445.86, 91.27) * mm, "end": v(445.84, 90.64) * mm});
            skLineSegment(sketch, "E1011", {"start": v(445.84, 90.64) * mm, "end": v(446.56, 89.92) * mm});
            skLineSegment(sketch, "E1012", {"start": v(446.56, 89.92) * mm, "end": v(446.56, 89.34) * mm});
            skLineSegment(sketch, "E1013", {"start": v(446.56, 89.34) * mm, "end": v(447.24, 88.78) * mm});
            skLineSegment(sketch, "E1014", {"start": v(447.24, 88.78) * mm, "end": v(447.24, 88.12) * mm});
            skLineSegment(sketch, "E1015", {"start": v(447.24, 88.12) * mm, "end": v(447.78, 87.51) * mm});
            skLineSegment(sketch, "E1016", {"start": v(447.78, 87.51) * mm, "end": v(447.78, 86.95) * mm});
            skLineSegment(sketch, "E1017", {"start": v(447.78, 86.95) * mm, "end": v(448.4, 86.27) * mm});
            skLineSegment(sketch, "E1018", {"start": v(448.4, 86.27) * mm, "end": v(449.01, 85.7) * mm});
            skLineSegment(sketch, "E1019", {"start": v(449.01, 85.7) * mm, "end": v(449.01, 84.83) * mm});
            skLineSegment(sketch, "E1020", {"start": v(449.01, 84.83) * mm, "end": v(449.62, 84.36) * mm});
            skLineSegment(sketch, "E1021", {"start": v(449.62, 84.36) * mm, "end": v(449.62, 83.76) * mm});
            skLineSegment(sketch, "E1022", {"start": v(449.62, 83.76) * mm, "end": v(450.93, 82.5) * mm});
            skLineSegment(sketch, "E1023", {"start": v(450.93, 82.5) * mm, "end": v(450.93, 81.83) * mm});
            skLineSegment(sketch, "E1024", {"start": v(450.93, 81.83) * mm, "end": v(452.25, 80.62) * mm});
            skLineSegment(sketch, "E1025", {"start": v(452.25, 80.62) * mm, "end": v(452.25, 80.01) * mm});
            skLineSegment(sketch, "E1026", {"start": v(452.25, 80.01) * mm, "end": v(454.1, 78.13) * mm});
            skLineSegment(sketch, "E1027", {"start": v(454.1, 78.13) * mm, "end": v(454.1, 77.53) * mm});
            skLineSegment(sketch, "E1028", {"start": v(454.1, 77.53) * mm, "end": v(456.66, 74.95) * mm});
            skLineSegment(sketch, "E1029", {"start": v(456.66, 74.95) * mm, "end": v(456.66, 74.4) * mm});
            skLineSegment(sketch, "E1030", {"start": v(456.66, 74.4) * mm, "end": v(460.94, 69.97) * mm});
            skLineSegment(sketch, "E1031", {"start": v(460.94, 69.97) * mm, "end": v(460.94, 69.37) * mm});
            skLineSegment(sketch, "E1032", {"start": v(460.94, 69.37) * mm, "end": v(464.1, 66.18) * mm});
            skLineSegment(sketch, "E1033", {"start": v(464.1, 66.18) * mm, "end": v(466, 64.35) * mm});
            skLineSegment(sketch, "E1034", {"start": v(466, 64.35) * mm, "end": v(466, 63.68) * mm});
            skLineSegment(sketch, "E1035", {"start": v(466, 63.68) * mm, "end": v(469.21, 60.6) * mm});
            skLineSegment(sketch, "E1036", {"start": v(469.21, 60.6) * mm, "end": v(469.75, 60.08) * mm});
            skLineSegment(sketch, "E1037", {"start": v(469.75, 60.08) * mm, "end": v(469.75, 59.32) * mm});
            skLineSegment(sketch, "E1038", {"start": v(469.75, 59.32) * mm, "end": v(471.6, 57.45) * mm});
            skLineSegment(sketch, "E1039", {"start": v(471.6, 57.45) * mm, "end": v(471.6, 56.87) * mm});
            skLineSegment(sketch, "E1040", {"start": v(471.6, 56.87) * mm, "end": v(474.72, 53.72) * mm});
            skLineSegment(sketch, "E1041", {"start": v(474.72, 53.72) * mm, "end": v(474.72, 53.17) * mm});
            skLineSegment(sketch, "E1042", {"start": v(474.72, 53.17) * mm, "end": v(479.17, 48.67) * mm});
            skLineSegment(sketch, "E1043", {"start": v(479.17, 48.67) * mm, "end": v(479.67, 48.62) * mm});
            skLineSegment(sketch, "E1044", {"start": v(479.67, 48.62) * mm, "end": v(481.72, 46.78) * mm});
            skLineSegment(sketch, "E1045", {"start": v(481.72, 46.78) * mm, "end": v(482.33, 46.78) * mm});
            skLineSegment(sketch, "E1046", {"start": v(482.33, 46.78) * mm, "end": v(482.9, 46.23) * mm});
            skLineSegment(sketch, "E1047", {"start": v(482.9, 46.23) * mm, "end": v(484.84, 46.23) * mm});
            skLineSegment(sketch, "E1048", {"start": v(484.84, 46.23) * mm, "end": v(485.51, 45.58) * mm});
            skLineSegment(sketch, "E1049", {"start": v(485.51, 45.58) * mm, "end": v(487.94, 45.58) * mm});
            skLineSegment(sketch, "E1050", {"start": v(487.94, 45.58) * mm, "end": v(488.6, 44.83) * mm});
            skLineSegment(sketch, "E1051", {"start": v(488.6, 44.83) * mm, "end": v(488.6, 44.28) * mm});
            skLineSegment(sketch, "E1052", {"start": v(488.6, 44.28) * mm, "end": v(366.23, 44.34) * mm});
            skSolve(sketch);
        }
        {
            var Q0;
            {var subQ1=sQuery(id+"F0.wireOp",EDGE,"E393");Q0=makeQuery(id+"F0.imprint","IMPRINT",FACE,{"disambiguationData":[TD([[makeQuery(id+"F0.imprint","IMPRINT",EDGE,{"derivedFrom":subQ1}),-1.0]])]});}
            var Q1;
            {var subQ0=sQuery(id+"F0.wireOp",EDGE,"E393");Q1=makeQuery(id+"F0.imprint","IMPRINT",FACE,{"disambiguationData":[TD([[makeQuery(id+"F0.imprint","IMPRINT",EDGE,{"derivedFrom":subQ0}),1.0]])]});}
            extrude(context, id + "F1", {"entities" : qUnion([Q0, Q1]), "depth" : 1 * mm, "offsetDistance" : 25 * mm});
        }
        {
            var Q0;
            {var subQ1=sQuery(id+"F0.wireOp",EDGE,"E1");Q0=makeQuery(id+"F0.imprint","IMPRINT",FACE,{"disambiguationData":[TD([[makeQuery(id+"F0.imprint","IMPRINT",EDGE,{"derivedFrom":subQ1}),-1.0]])]});}
            var Q1;
            {var subQ4=sQuery(id+"F0.wireOp",EDGE,"E207");Q1=makeQuery(id+"F0.imprint","IMPRINT",FACE,{"disambiguationData":[TD([[makeQuery(id+"F0.imprint","IMPRINT",EDGE,{"derivedFrom":subQ4}),-1.0]])]});}
            extrude(context, id + "F2", {"entities" : qUnion([Q0, Q1]), "depth" : 1 * mm, "offsetDistance" : 25 * mm});
        }
    });
